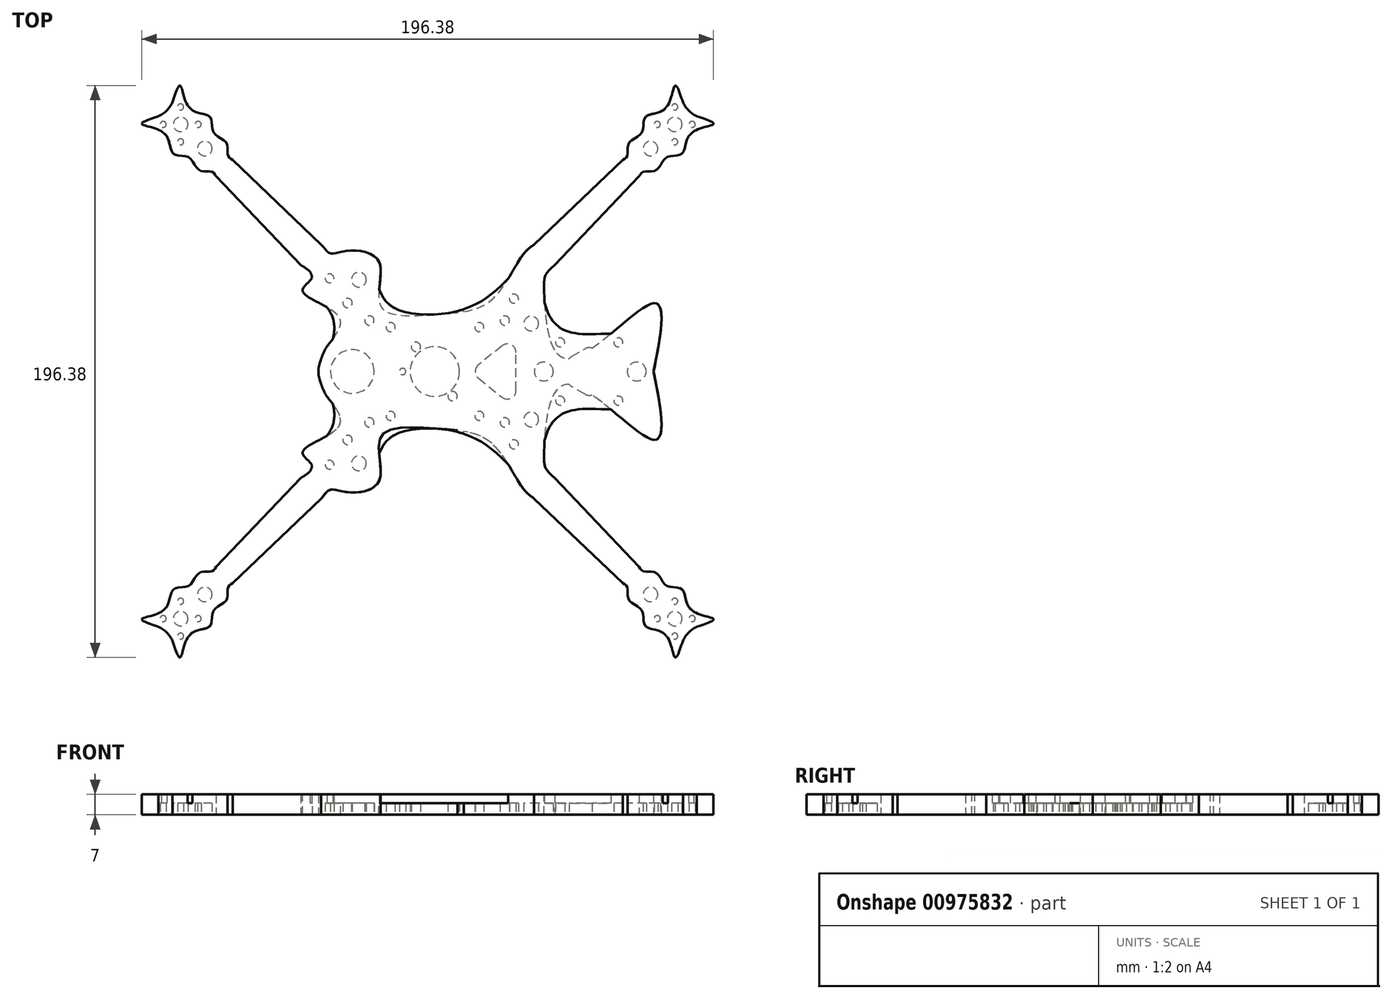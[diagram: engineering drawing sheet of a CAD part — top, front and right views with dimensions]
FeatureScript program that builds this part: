
annotation { "Feature Type Name" : "Feature", "Feature Type Description" : "" }
export const myFeature = defineFeature(function(context is Context, id is Id, definition is map)
    precondition{}
    {
        {
            var Q0;
            Q0=qCreatedBy(makeId("Top.planeOp"),FACE);
            var sketch = newSketch(context, id + "F0", { "sketchPlane" : qUnion([Q0])});
            skCircle(sketch, "E0", {"center": v(-32.76, 31.1) * mm, "radius": 1.46 * mm});
            skCircle(sketch, "E1", {"center": v(-32.76, -31.1) * mm, "radius": 1.46 * mm});
            skCircle(sketch, "E2", {"center": v(28.8, -24.3) * mm, "radius": 1.5 * mm});
            skCircle(sketch, "E3", {"center": v(28.8, 24.3) * mm, "radius": 1.5 * mm});
            skCircle(sketch, "E4", {"center": v(38.75, 0) * mm, "radius": 3.16 * mm});
            skCircle(sketch, "E5", {"center": v(69.82, 0) * mm, "radius": 3.16 * mm});
            skCircle(sketch, "E6", {"center": v(63.67, -9.72) * mm, "radius": 1.5 * mm});
            skCircle(sketch, "E7", {"center": v(63.67, 9.72) * mm, "radius": 1.5 * mm});
            skCircle(sketch, "E8", {"center": v(44.23, 9.72) * mm, "radius": 1.5 * mm});
            skCircle(sketch, "E9", {"center": v(44.23, -9.72) * mm, "radius": 1.5 * mm});
            skCircle(sketch, "E10", {"center": v(-76.65, 82.48) * mm, "radius": 1.02 * mm});
            skCircle(sketch, "E11", {"center": v(-82.48, 88.32) * mm, "radius": 1.02 * mm});
            skCircle(sketch, "E12", {"center": v(-88.32, 82.48) * mm, "radius": 1.02 * mm});
            skCircle(sketch, "E13", {"center": v(-82.48, 82.48) * mm, "radius": 2.43 * mm});
            skCircle(sketch, "E14", {"center": v(-82.48, 76.65) * mm, "radius": 1.02 * mm});
            skCircle(sketch, "E15", {"center": v(-74.4, 74.4) * mm, "radius": 2.43 * mm});
            skCircle(sketch, "E16", {"center": v(88.32, 82.48) * mm, "radius": 1.02 * mm});
            skCircle(sketch, "E17", {"center": v(82.48, 88.32) * mm, "radius": 1.02 * mm});
            skCircle(sketch, "E18", {"center": v(76.65, 82.48) * mm, "radius": 1.02 * mm});
            skCircle(sketch, "E19", {"center": v(82.48, 82.48) * mm, "radius": 2.43 * mm});
            skCircle(sketch, "E20", {"center": v(74.4, 74.4) * mm, "radius": 2.43 * mm});
            skCircle(sketch, "E21", {"center": v(82.48, 76.65) * mm, "radius": 1.02 * mm});
            skCircle(sketch, "E22", {"center": v(76.65, -82.48) * mm, "radius": 1.02 * mm});
            skCircle(sketch, "E23", {"center": v(74.4, -74.4) * mm, "radius": 2.43 * mm});
            skCircle(sketch, "E24", {"center": v(82.48, -76.65) * mm, "radius": 1.02 * mm});
            skCircle(sketch, "E25", {"center": v(82.48, -82.48) * mm, "radius": 2.43 * mm});
            skCircle(sketch, "E26", {"center": v(88.32, -82.48) * mm, "radius": 1.02 * mm});
            skCircle(sketch, "E27", {"center": v(82.48, -88.32) * mm, "radius": 1.02 * mm});
            skCircle(sketch, "E28", {"center": v(-25.16, 0) * mm, "radius": 7.3 * mm});
            skCircle(sketch, "E29", {"center": v(17.68, -15.25) * mm, "radius": 1.5 * mm});
            skCircle(sketch, "E30", {"center": v(17.68, 15.25) * mm, "radius": 1.5 * mm});
            skCircle(sketch, "E31", {"center": v(-12.82, 15.25) * mm, "radius": 1.5 * mm});
            skCircle(sketch, "E32", {"center": v(-12.82, -15.25) * mm, "radius": 1.5 * mm});
            skCircle(sketch, "E33", {"center": v(-26.73, 22.84) * mm, "radius": 1.6 * mm});
            skCircle(sketch, "E34", {"center": v(-26.73, -22.84) * mm, "radius": 1.6 * mm});
            skCircle(sketch, "E35", {"center": v(-22.98, -30.67) * mm, "radius": 2.47 * mm});
            skCircle(sketch, "E36", {"center": v(34.56, -16) * mm, "radius": 2.47 * mm});
            skCircle(sketch, "E37", {"center": v(34.56, 16) * mm, "radius": 2.47 * mm});
            skCircle(sketch, "E38", {"center": v(-22.98, 30.67) * mm, "radius": 2.47 * mm});
            skCircle(sketch, "E39", {"center": v(-19.44, 17.01) * mm, "radius": 1.6 * mm});
            skCircle(sketch, "E40", {"center": v(25.76, 17.01) * mm, "radius": 1.6 * mm});
            skCircle(sketch, "E41", {"center": v(25.76, -17.01) * mm, "radius": 1.6 * mm});
            skCircle(sketch, "E42", {"center": v(-19.44, -17.01) * mm, "radius": 1.6 * mm});
            skCircle(sketch, "E43", {"center": v(-74.4, -74.4) * mm, "radius": 2.43 * mm});
            skCircle(sketch, "E44", {"center": v(-82.48, -88.32) * mm, "radius": 1.02 * mm});
            skCircle(sketch, "E45", {"center": v(-88.32, -82.48) * mm, "radius": 1.02 * mm});
            skCircle(sketch, "E46", {"center": v(-82.48, -76.65) * mm, "radius": 1.02 * mm});
            skCircle(sketch, "E47", {"center": v(-82.48, -82.48) * mm, "radius": 2.43 * mm});
            skCircle(sketch, "E48", {"center": v(-76.65, -82.48) * mm, "radius": 1.02 * mm});
            skLineSegment(sketch, "E49", {"start": v(0.97, -7.58) * mm, "end": v(-3.4, -5.05) * mm, "construction": true});
            skLineSegment(sketch, "E50", {"start": v(8.26, -5.05) * mm, "end": v(3.89, -7.58) * mm, "construction": true});
            skLineSegment(sketch, "E51", {"start": v(9.72, 2.53) * mm, "end": v(9.72, -2.53) * mm, "construction": true});
            skLineSegment(sketch, "E52", {"start": v(3.89, 7.58) * mm, "end": v(8.26, 5.05) * mm, "construction": true});
            skLineSegment(sketch, "E53", {"start": v(-3.4, 5.05) * mm, "end": v(0.97, 7.58) * mm, "construction": true});
            skLineSegment(sketch, "E54", {"start": v(-4.86, -2.53) * mm, "end": v(-4.86, 2.53) * mm, "construction": true});
            skLineSegment(sketch, "E55", {"start": v(-42.4, 35.54) * mm, "end": v(-70.64, 65.14) * mm});
            skLineSegment(sketch, "E56", {"start": v(-65.14, 70.64) * mm, "end": v(-35.54, 42.4) * mm});
            skLineSegment(sketch, "E57", {"start": v(35.54, 42.4) * mm, "end": v(65.14, 70.64) * mm});
            skLineSegment(sketch, "E58", {"start": v(70.64, 65.14) * mm, "end": v(42.4, 35.54) * mm});
            skLineSegment(sketch, "E59", {"start": v(42.4, -35.54) * mm, "end": v(70.64, -65.14) * mm});
            skLineSegment(sketch, "E60", {"start": v(65.14, -70.64) * mm, "end": v(35.54, -42.4) * mm});
            skLineSegment(sketch, "E61", {"start": v(-35.54, -42.4) * mm, "end": v(-65.14, -70.64) * mm});
            skLineSegment(sketch, "E62", {"start": v(-70.64, -65.14) * mm, "end": v(-42.4, -35.54) * mm});
            skLineSegment(sketch, "E63", {"start": v(52.5, -7.58) * mm, "end": v(48.12, -5.05) * mm});
            skLineSegment(sketch, "E64", {"start": v(59.78, -5.05) * mm, "end": v(55.4, -7.58) * mm});
            skLineSegment(sketch, "E65", {"start": v(61.24, 2.53) * mm, "end": v(61.24, -2.53) * mm});
            skLineSegment(sketch, "E66", {"start": v(55.4, 7.58) * mm, "end": v(59.78, 5.05) * mm});
            skLineSegment(sketch, "E67", {"start": v(48.12, 5.05) * mm, "end": v(52.5, 7.58) * mm});
            skLineSegment(sketch, "E68", {"start": v(46.66, -2.53) * mm, "end": v(46.66, 2.53) * mm});
            skLineSegment(sketch, "E69", {"start": v(24.77, 8.56) * mm, "end": v(16.99, 2.27) * mm});
            skLineSegment(sketch, "E70", {"start": v(16.99, -2.27) * mm, "end": v(24.77, -8.56) * mm});
            skLineSegment(sketch, "E71", {"start": v(29.52, -6.29) * mm, "end": v(29.52, 6.29) * mm});
            skArc(sketch, "E72", {"start": v(-4.86, -2.53) * mm, "mid": v(-4.47, -3.98) * mm, "end": v(-3.4, -5.05) * mm, "construction": true});
            skArc(sketch, "E73", {"start": v(0.97, -7.58) * mm, "mid": v(2.43, -7.97) * mm, "end": v(3.89, -7.58) * mm, "construction": true});
            skArc(sketch, "E74", {"start": v(8.26, -5.05) * mm, "mid": v(9.33, -3.98) * mm, "end": v(9.72, -2.53) * mm, "construction": true});
            skArc(sketch, "E75", {"start": v(9.72, 2.53) * mm, "mid": v(9.33, 3.98) * mm, "end": v(8.26, 5.05) * mm, "construction": true});
            skArc(sketch, "E76", {"start": v(3.89, 7.58) * mm, "mid": v(2.43, 7.97) * mm, "end": v(0.97, 7.58) * mm, "construction": true});
            skArc(sketch, "E77", {"start": v(-3.4, 5.05) * mm, "mid": v(-4.47, 3.98) * mm, "end": v(-4.86, 2.53) * mm, "construction": true});
            skArc(sketch, "E78", {"start": v(-89.87, 85.21) * mm, "mid": v(-87.13, 87.13) * mm, "end": v(-85.21, 89.87) * mm});
            skArc(sketch, "E79", {"start": v(85.21, 89.87) * mm, "mid": v(87.13, 87.13) * mm, "end": v(89.87, 85.21) * mm});
            skArc(sketch, "E80", {"start": v(89.87, -85.21) * mm, "mid": v(87.13, -87.13) * mm, "end": v(85.21, -89.87) * mm});
            skArc(sketch, "E81", {"start": v(-85.21, -89.87) * mm, "mid": v(-87.13, -87.13) * mm, "end": v(-89.87, -85.21) * mm});
            skArc(sketch, "E82", {"start": v(-35.56, 4.15) * mm, "mid": v(-36.49, 0) * mm, "end": v(-35.56, -4.15) * mm});
            skArc(sketch, "E83", {"start": v(46.66, -2.53) * mm, "mid": v(47.05, -3.98) * mm, "end": v(48.12, -5.05) * mm});
            skArc(sketch, "E84", {"start": v(52.5, -7.58) * mm, "mid": v(53.95, -7.97) * mm, "end": v(55.4, -7.58) * mm});
            skArc(sketch, "E85", {"start": v(59.78, -5.05) * mm, "mid": v(60.85, -3.98) * mm, "end": v(61.24, -2.53) * mm});
            skArc(sketch, "E86", {"start": v(61.24, 2.53) * mm, "mid": v(60.85, 3.98) * mm, "end": v(59.78, 5.05) * mm});
            skArc(sketch, "E87", {"start": v(55.4, 7.58) * mm, "mid": v(53.95, 7.97) * mm, "end": v(52.5, 7.58) * mm});
            skArc(sketch, "E88", {"start": v(48.12, 5.05) * mm, "mid": v(47.05, 3.98) * mm, "end": v(46.66, 2.53) * mm});
            skArc(sketch, "E89", {"start": v(29.52, 6.29) * mm, "mid": v(27.86, 8.92) * mm, "end": v(24.77, 8.56) * mm});
            skArc(sketch, "E90", {"start": v(16.99, 2.27) * mm, "mid": v(15.9, 0) * mm, "end": v(16.99, -2.27) * mm});
            skArc(sketch, "E91", {"start": v(24.77, -8.56) * mm, "mid": v(27.86, -8.92) * mm, "end": v(29.52, -6.29) * mm});
            skFitSpline(sketch, "E92", {"points": [v(-70.64, 65.14) * mm, v(-72.1, 66.67) * mm, v(-76.27, 67.2) * mm, v(-79.78, 71.48) * mm, v(-84.93, 72.72) * mm, v(-87.81, 79.4) * mm, v(-95.41, 82.6) * mm, v(-89.87, 85.21) * mm]});
            skFitSpline(sketch, "E93", {"points": [v(-85.21, 89.87) * mm, v(-82.6, 95.41) * mm, v(-79.4, 87.81) * mm, v(-72.72, 84.93) * mm, v(-71.48, 79.78) * mm, v(-67.2, 76.27) * mm, v(-66.67, 72.1) * mm, v(-65.14, 70.64) * mm]});
            skFitSpline(sketch, "E94", {"points": [v(-35.53, 42.41) * mm, v(-32.44, 39.47) * mm, v(-27.5, 40.23) * mm, v(-16.3, 36.82) * mm, v(-15.63, 21.83) * mm, v(3.2, 19.1) * mm, v(21.3, 23.94) * mm, v(31.5, 38.64) * mm, v(35.55, 42.52) * mm]});
            skFitSpline(sketch, "E95", {"points": [v(65.14, 70.64) * mm, v(66.67, 72.1) * mm, v(67.2, 76.27) * mm, v(71.48, 79.78) * mm, v(72.72, 84.93) * mm, v(79.4, 87.81) * mm, v(82.6, 95.41) * mm, v(85.21, 89.87) * mm]});
            skFitSpline(sketch, "E96", {"points": [v(89.87, 85.21) * mm, v(95.41, 82.6) * mm, v(87.81, 79.4) * mm, v(84.93, 72.72) * mm, v(79.78, 71.48) * mm, v(76.27, 67.2) * mm, v(72.1, 66.67) * mm, v(70.64, 65.14) * mm]});
            skFitSpline(sketch, "E97", {"points": [v(42.4, 35.54) * mm, v(39.6, 32.6) * mm, v(38.88, 26.27) * mm, v(46.07, 4.37) * mm, v(75.44, 22.8) * mm, v(75.44, 0) * mm]});
            skFitSpline(sketch, "E98", {"points": [v(75.44, 0) * mm, v(75.44, -22.8) * mm, v(46.07, -4.37) * mm, v(38.88, -26.27) * mm, v(39.6, -32.6) * mm, v(42.4, -35.54) * mm]});
            skFitSpline(sketch, "E99", {"points": [v(70.64, -65.14) * mm, v(72.1, -66.67) * mm, v(76.27, -67.2) * mm, v(79.78, -71.48) * mm, v(84.93, -72.72) * mm, v(87.81, -79.4) * mm, v(95.41, -82.6) * mm, v(89.87, -85.21) * mm]});
            skFitSpline(sketch, "E100", {"points": [v(85.21, -89.87) * mm, v(82.6, -95.41) * mm, v(79.4, -87.81) * mm, v(72.72, -84.93) * mm, v(71.48, -79.78) * mm, v(67.2, -76.27) * mm, v(66.67, -72.1) * mm, v(65.14, -70.64) * mm]});
            skFitSpline(sketch, "E101", {"points": [v(35.54, -42.4) * mm, v(31.48, -38.53) * mm, v(21.27, -23.86) * mm, v(3.16, -19.04) * mm, v(-15.67, -21.8) * mm, v(-16.31, -36.79) * mm, v(-27.5, -40.21) * mm, v(-32.45, -39.46) * mm, v(-35.54, -42.4) * mm]});
            skFitSpline(sketch, "E102", {"points": [v(-65.14, -70.64) * mm, v(-66.67, -72.1) * mm, v(-67.2, -76.27) * mm, v(-71.48, -79.78) * mm, v(-72.72, -84.93) * mm, v(-79.4, -87.81) * mm, v(-82.6, -95.41) * mm, v(-85.21, -89.87) * mm]});
            skFitSpline(sketch, "E103", {"points": [v(-89.87, -85.21) * mm, v(-95.41, -82.6) * mm, v(-87.81, -79.4) * mm, v(-84.93, -72.72) * mm, v(-79.78, -71.48) * mm, v(-76.27, -67.2) * mm, v(-72.1, -66.67) * mm, v(-70.64, -65.14) * mm]});
            skFitSpline(sketch, "E104", {"points": [v(-42.4, -35.54) * mm, v(-38.56, -31.5) * mm, v(-41.74, -26.82) * mm, v(-29.39, -17.9) * mm, v(-33.52, -8.47) * mm, v(-35.56, -4.15) * mm]});
            skFitSpline(sketch, "E105", {"points": [v(-35.56, 4.15) * mm, v(-33.52, 8.47) * mm, v(-29.39, 17.9) * mm, v(-41.74, 26.82) * mm, v(-38.56, 31.5) * mm, v(-42.4, 35.54) * mm]});
            skLineSegment(sketch, "E106", {"start": v(-1.94, 2.53) * mm, "end": v(6.8, -2.53) * mm, "construction": true});
            skLineSegment(sketch, "E107", {"start": v(-1.94, -2.53) * mm, "end": v(6.8, 2.53) * mm, "construction": true});
            skLineSegment(sketch, "E108", {"start": v(2.43, 5.05) * mm, "end": v(2.43, -5.05) * mm, "construction": true});
            skPoint(sketch, "E109", {"position": v(2.43, 0) * mm});
            skCircle(sketch, "E110", {"center": v(2.43, 0) * mm, "radius": 8.5 * mm});
            skLineSegment(sketch, "E111", {"start": v(-12.82, 15.25) * mm, "end": v(17.68, -15.25) * mm, "construction": true});
            skLineSegment(sketch, "E112", {"start": v(-12.82, -15.25) * mm, "end": v(17.68, 15.25) * mm, "construction": true});
            skLineSegment(sketch, "E113", {"start": v(-12.82, 15.25) * mm, "end": v(17.68, 15.25) * mm, "construction": true});
            skLineSegment(sketch, "E114", {"start": v(17.68, 15.25) * mm, "end": v(17.68, -15.25) * mm, "construction": true});
            skLineSegment(sketch, "E115.bottom", {"start": v(-6.59, 11.05) * mm, "end": v(13.31, 11.05) * mm, "construction": true});
            skLineSegment(sketch, "E115.top", {"start": v(-6.59, -11.05) * mm, "end": v(13.31, -11.05) * mm, "construction": true});
            skLineSegment(sketch, "E115.left", {"start": v(-6.59, 11.05) * mm, "end": v(-6.59, -11.05) * mm, "construction": true});
            skLineSegment(sketch, "E115.right", {"start": v(13.31, 11.05) * mm, "end": v(13.31, -11.05) * mm, "construction": true});
            skPoint(sketch, "E116", {"position": v(-6.59, 0) * mm});
            skCircle(sketch, "E117", {"center": v(-4.05, 8.5) * mm, "radius": 1.6 * mm});
            skCircle(sketch, "E118", {"center": v(8.55, -8.5) * mm, "radius": 1.6 * mm});
            skPoint(sketch, "E119", {"position": v(-14.67, 26.96) * mm});
            skPoint(sketch, "E120", {"position": v(-14.67, -26.85) * mm});
            skLineSegment(sketch, "E121", {"start": v(-14.67, 26.96) * mm, "end": v(-14.67, -26.85) * mm, "construction": true});
            skFitSpline(sketch, "E122", {"points": [v(-14.67, 26.96) * mm, v(12.39, 26.96) * mm, v(35.54, 42.4) * mm], "startDerivative": vector(9.65, -21.34) * mm, "endDerivative": vector(35.23, 30.54) * mm});
            skFitSpline(sketch, "E123.MirrorCS", {"points": [v(-14.67, -26.96) * mm, v(12.39, -26.96) * mm, v(35.54, -42.4) * mm], "startDerivative": vector(9.65, 21.34) * mm, "endDerivative": vector(35.23, -30.54) * mm});
            skCircle(sketch, "E124", {"center": v(7.43, 20) * mm, "radius": 1.1 * mm});
            skCircle(sketch, "E125", {"center": v(-12.57, 0) * mm, "radius": 1.1 * mm});
            skCircle(sketch, "E126", {"center": v(7.43, -20) * mm, "radius": 1.1 * mm});
            skSolve(sketch);
        }
        {
            var Q0;
            Q0=qCreatedBy(makeId("Top.planeOp"),FACE);
            var sketch = newSketch(context, id + "F1", { "sketchPlane" : qUnion([Q0])});
            skCircle(sketch, "E127", {"center": v(-33.7, 32) * mm, "radius": 1.5 * mm});
            skCircle(sketch, "E128", {"center": v(-33.7, -32) * mm, "radius": 1.5 * mm});
            skCircle(sketch, "E129", {"center": v(29.62, -25) * mm, "radius": 1.55 * mm});
            skCircle(sketch, "E130", {"center": v(29.62, 25) * mm, "radius": 1.55 * mm});
            skCircle(sketch, "E131", {"center": v(39.86, 0) * mm, "radius": 3.25 * mm});
            skCircle(sketch, "E132", {"center": v(71.83, 0) * mm, "radius": 3.25 * mm});
            skCircle(sketch, "E133", {"center": v(65.5, -10) * mm, "radius": 1.55 * mm});
            skCircle(sketch, "E134", {"center": v(65.5, 10) * mm, "radius": 1.55 * mm});
            skCircle(sketch, "E135", {"center": v(45.5, 10) * mm, "radius": 1.55 * mm});
            skCircle(sketch, "E136", {"center": v(45.5, -10) * mm, "radius": 1.55 * mm});
            skCircle(sketch, "E137", {"center": v(-78.85, 84.85) * mm, "radius": 1.05 * mm});
            skCircle(sketch, "E138", {"center": v(-84.85, 90.85) * mm, "radius": 1.05 * mm});
            skCircle(sketch, "E139", {"center": v(-90.85, 84.85) * mm, "radius": 1.05 * mm});
            skCircle(sketch, "E140", {"center": v(-84.85, 84.85) * mm, "radius": 2.5 * mm});
            skCircle(sketch, "E141", {"center": v(-84.85, 78.85) * mm, "radius": 1.05 * mm});
            skCircle(sketch, "E142", {"center": v(-76.54, 76.54) * mm, "radius": 2.5 * mm});
            skCircle(sketch, "E143", {"center": v(90.85, 84.85) * mm, "radius": 1.05 * mm});
            skCircle(sketch, "E144", {"center": v(84.85, 90.85) * mm, "radius": 1.05 * mm});
            skCircle(sketch, "E145", {"center": v(78.85, 84.85) * mm, "radius": 1.05 * mm});
            skCircle(sketch, "E146", {"center": v(84.85, 84.85) * mm, "radius": 2.5 * mm});
            skCircle(sketch, "E147", {"center": v(76.54, 76.54) * mm, "radius": 2.5 * mm});
            skCircle(sketch, "E148", {"center": v(84.85, 78.85) * mm, "radius": 1.05 * mm});
            skCircle(sketch, "E149", {"center": v(78.85, -84.85) * mm, "radius": 1.05 * mm});
            skCircle(sketch, "E150", {"center": v(76.54, -76.54) * mm, "radius": 2.5 * mm});
            skCircle(sketch, "E151", {"center": v(84.85, -78.85) * mm, "radius": 1.05 * mm});
            skCircle(sketch, "E152", {"center": v(84.85, -84.85) * mm, "radius": 2.5 * mm});
            skCircle(sketch, "E153", {"center": v(90.85, -84.85) * mm, "radius": 1.05 * mm});
            skCircle(sketch, "E154", {"center": v(84.85, -90.85) * mm, "radius": 1.05 * mm});
            skCircle(sketch, "E155", {"center": v(-25.89, 0) * mm, "radius": 7.5 * mm});
            skCircle(sketch, "E156", {"center": v(17.75, -15.25) * mm, "radius": 1.55 * mm});
            skCircle(sketch, "E157", {"center": v(17.75, 15.25) * mm, "radius": 1.55 * mm});
            skCircle(sketch, "E158", {"center": v(-12.75, 15.25) * mm, "radius": 1.55 * mm});
            skCircle(sketch, "E159", {"center": v(-12.75, -15.25) * mm, "radius": 1.55 * mm});
            skCircle(sketch, "E160", {"center": v(-27.5, 23.5) * mm, "radius": 1.6 * mm});
            skCircle(sketch, "E161", {"center": v(-27.5, -23.5) * mm, "radius": 1.6 * mm});
            skCircle(sketch, "E162", {"center": v(-23.64, -31.55) * mm, "radius": 2.54 * mm});
            skCircle(sketch, "E163", {"center": v(35.56, -16.47) * mm, "radius": 2.54 * mm});
            skCircle(sketch, "E164", {"center": v(35.56, 16.47) * mm, "radius": 2.54 * mm});
            skCircle(sketch, "E165", {"center": v(-23.64, 31.55) * mm, "radius": 2.54 * mm});
            skCircle(sketch, "E166", {"center": v(-20, 17.5) * mm, "radius": 1.6 * mm});
            skCircle(sketch, "E167", {"center": v(26.5, 17.5) * mm, "radius": 1.6 * mm});
            skCircle(sketch, "E168", {"center": v(26.5, -17.5) * mm, "radius": 1.6 * mm});
            skCircle(sketch, "E169", {"center": v(-20, -17.5) * mm, "radius": 1.6 * mm});
            skCircle(sketch, "E170", {"center": v(-76.54, -76.54) * mm, "radius": 2.5 * mm});
            skCircle(sketch, "E171", {"center": v(-84.85, -90.85) * mm, "radius": 1.05 * mm});
            skCircle(sketch, "E172", {"center": v(-90.85, -84.85) * mm, "radius": 1.05 * mm});
            skCircle(sketch, "E173", {"center": v(-84.85, -78.85) * mm, "radius": 1.05 * mm});
            skCircle(sketch, "E174", {"center": v(-84.85, -84.85) * mm, "radius": 2.5 * mm});
            skCircle(sketch, "E175", {"center": v(-78.85, -84.85) * mm, "radius": 1.05 * mm});
            skLineSegment(sketch, "E176", {"start": v(1, -7.8) * mm, "end": v(-3.5, -5.2) * mm, "construction": true});
            skLineSegment(sketch, "E177", {"start": v(8.5, -5.2) * mm, "end": v(4, -7.8) * mm, "construction": true});
            skLineSegment(sketch, "E178", {"start": v(10, 2.6) * mm, "end": v(10, -2.6) * mm, "construction": true});
            skLineSegment(sketch, "E179", {"start": v(4, 7.8) * mm, "end": v(8.5, 5.2) * mm, "construction": true});
            skLineSegment(sketch, "E180", {"start": v(-3.5, 5.2) * mm, "end": v(1, 7.8) * mm, "construction": true});
            skLineSegment(sketch, "E181", {"start": v(-5, -2.6) * mm, "end": v(-5, 2.6) * mm, "construction": true});
            skLineSegment(sketch, "E182", {"start": v(-43.63, 36.56) * mm, "end": v(-72.67, 67) * mm});
            skLineSegment(sketch, "E183", {"start": v(-67, 72.67) * mm, "end": v(-36.56, 43.63) * mm});
            skLineSegment(sketch, "E184", {"start": v(36.56, 43.63) * mm, "end": v(67, 72.67) * mm});
            skLineSegment(sketch, "E185", {"start": v(72.67, 67) * mm, "end": v(43.63, 36.56) * mm});
            skLineSegment(sketch, "E186", {"start": v(43.63, -36.56) * mm, "end": v(72.67, -67) * mm});
            skLineSegment(sketch, "E187", {"start": v(67, -72.67) * mm, "end": v(36.56, -43.63) * mm});
            skLineSegment(sketch, "E188", {"start": v(-36.56, -43.63) * mm, "end": v(-67, -72.67) * mm});
            skLineSegment(sketch, "E189", {"start": v(-72.67, -67) * mm, "end": v(-43.63, -36.56) * mm});
            skLineSegment(sketch, "E190", {"start": v(54, -7.8) * mm, "end": v(49.5, -5.2) * mm});
            skLineSegment(sketch, "E191", {"start": v(61.5, -5.2) * mm, "end": v(57, -7.8) * mm});
            skLineSegment(sketch, "E192", {"start": v(63, 2.6) * mm, "end": v(63, -2.6) * mm});
            skLineSegment(sketch, "E193", {"start": v(57, 7.8) * mm, "end": v(61.5, 5.2) * mm});
            skLineSegment(sketch, "E194", {"start": v(49.5, 5.2) * mm, "end": v(54, 7.8) * mm});
            skLineSegment(sketch, "E195", {"start": v(48, -2.6) * mm, "end": v(48, 2.6) * mm});
            skLineSegment(sketch, "E196", {"start": v(25.48, 8.8) * mm, "end": v(17.47, 2.33) * mm});
            skLineSegment(sketch, "E197", {"start": v(17.47, -2.33) * mm, "end": v(25.48, -8.8) * mm});
            skLineSegment(sketch, "E198", {"start": v(30.37, -6.47) * mm, "end": v(30.37, 6.47) * mm});
            skArc(sketch, "E199", {"start": v(-5, -2.6) * mm, "mid": v(-4.6, -4.1) * mm, "end": v(-3.5, -5.2) * mm, "construction": true});
            skArc(sketch, "E200", {"start": v(1, -7.8) * mm, "mid": v(2.5, -8.2) * mm, "end": v(4, -7.8) * mm, "construction": true});
            skArc(sketch, "E201", {"start": v(8.5, -5.2) * mm, "mid": v(9.6, -4.1) * mm, "end": v(10, -2.6) * mm, "construction": true});
            skArc(sketch, "E202", {"start": v(10, 2.6) * mm, "mid": v(9.6, 4.1) * mm, "end": v(8.5, 5.2) * mm, "construction": true});
            skArc(sketch, "E203", {"start": v(4, 7.8) * mm, "mid": v(2.5, 8.2) * mm, "end": v(1, 7.8) * mm, "construction": true});
            skArc(sketch, "E204", {"start": v(-3.5, 5.2) * mm, "mid": v(-4.6, 4.1) * mm, "end": v(-5, 2.6) * mm, "construction": true});
            skArc(sketch, "E205", {"start": v(-92.45, 87.66) * mm, "mid": v(-89.64, 89.64) * mm, "end": v(-87.66, 92.45) * mm});
            skArc(sketch, "E206", {"start": v(87.66, 92.45) * mm, "mid": v(89.64, 89.64) * mm, "end": v(92.45, 87.66) * mm});
            skArc(sketch, "E207", {"start": v(92.45, -87.66) * mm, "mid": v(89.64, -89.64) * mm, "end": v(87.66, -92.45) * mm});
            skArc(sketch, "E208", {"start": v(-87.66, -92.45) * mm, "mid": v(-89.64, -89.64) * mm, "end": v(-92.45, -87.66) * mm});
            skArc(sketch, "E209", {"start": v(-36.58, 4.27) * mm, "mid": v(-37.53, 0) * mm, "end": v(-36.58, -4.27) * mm});
            skArc(sketch, "E210", {"start": v(48, -2.6) * mm, "mid": v(48.4, -4.1) * mm, "end": v(49.5, -5.2) * mm});
            skArc(sketch, "E211", {"start": v(54, -7.8) * mm, "mid": v(55.5, -8.2) * mm, "end": v(57, -7.8) * mm});
            skArc(sketch, "E212", {"start": v(61.5, -5.2) * mm, "mid": v(62.6, -4.1) * mm, "end": v(63, -2.6) * mm});
            skArc(sketch, "E213", {"start": v(63, 2.6) * mm, "mid": v(62.6, 4.1) * mm, "end": v(61.5, 5.2) * mm});
            skArc(sketch, "E214", {"start": v(57, 7.8) * mm, "mid": v(55.5, 8.2) * mm, "end": v(54, 7.8) * mm});
            skArc(sketch, "E215", {"start": v(49.5, 5.2) * mm, "mid": v(48.4, 4.1) * mm, "end": v(48, 2.6) * mm});
            skArc(sketch, "E216", {"start": v(30.37, 6.47) * mm, "mid": v(28.66, 9.18) * mm, "end": v(25.48, 8.8) * mm});
            skArc(sketch, "E217", {"start": v(17.47, 2.33) * mm, "mid": v(16.36, 0) * mm, "end": v(17.47, -2.33) * mm});
            skArc(sketch, "E218", {"start": v(25.48, -8.8) * mm, "mid": v(28.66, -9.18) * mm, "end": v(30.37, -6.47) * mm});
            skFitSpline(sketch, "E219", {"points": [v(-72.67, 67) * mm, v(-74.17, 68.59) * mm, v(-78.46, 69.14) * mm, v(-82.07, 73.54) * mm, v(-87.37, 74.8) * mm, v(-90.34, 81.69) * mm, v(-98.15, 84.97) * mm, v(-92.45, 87.66) * mm]});
            skFitSpline(sketch, "E220", {"points": [v(-87.66, 92.45) * mm, v(-84.97, 98.15) * mm, v(-81.69, 90.34) * mm, v(-74.8, 87.37) * mm, v(-73.54, 82.07) * mm, v(-69.14, 78.46) * mm, v(-68.59, 74.17) * mm, v(-67, 72.67) * mm]});
            skFitSpline(sketch, "E221", {"points": [v(-36.56, 43.63) * mm, v(-33.38, 40.6) * mm, v(-28.3, 41.37) * mm, v(-16.78, 37.85) * mm, v(-16.12, 22.42) * mm, v(3.25, 19.6) * mm, v(21.88, 24.54) * mm, v(32.38, 39.64) * mm, v(36.56, 43.63) * mm]});
            skFitSpline(sketch, "E222", {"points": [v(67, 72.67) * mm, v(68.59, 74.17) * mm, v(69.14, 78.46) * mm, v(73.54, 82.07) * mm, v(74.8, 87.37) * mm, v(81.69, 90.34) * mm, v(84.97, 98.15) * mm, v(87.66, 92.45) * mm]});
            skFitSpline(sketch, "E223", {"points": [v(92.45, 87.66) * mm, v(98.15, 84.97) * mm, v(90.34, 81.69) * mm, v(87.37, 74.8) * mm, v(82.07, 73.54) * mm, v(78.46, 69.14) * mm, v(74.17, 68.59) * mm, v(72.67, 67) * mm]});
            skFitSpline(sketch, "E224", {"points": [v(43.63, 36.56) * mm, v(40.74, 33.53) * mm, v(40, 27.02) * mm, v(47.4, 4.5) * mm, v(77.6, 23.46) * mm, v(77.6, 0) * mm]});
            skFitSpline(sketch, "E225", {"points": [v(77.6, 0) * mm, v(77.6, -23.46) * mm, v(47.4, -4.5) * mm, v(40, -27.02) * mm, v(40.74, -33.53) * mm, v(43.63, -36.56) * mm]});
            skFitSpline(sketch, "E226", {"points": [v(72.67, -67) * mm, v(74.17, -68.59) * mm, v(78.46, -69.14) * mm, v(82.07, -73.54) * mm, v(87.37, -74.8) * mm, v(90.34, -81.69) * mm, v(98.15, -84.97) * mm, v(92.45, -87.66) * mm]});
            skFitSpline(sketch, "E227", {"points": [v(87.66, -92.45) * mm, v(84.97, -98.15) * mm, v(81.69, -90.34) * mm, v(74.8, -87.37) * mm, v(73.54, -82.07) * mm, v(69.14, -78.46) * mm, v(68.59, -74.17) * mm, v(67, -72.67) * mm]});
            skFitSpline(sketch, "E228", {"points": [v(36.56, -43.63) * mm, v(32.38, -39.64) * mm, v(21.88, -24.54) * mm, v(3.25, -19.6) * mm, v(-16.12, -22.42) * mm, v(-16.78, -37.85) * mm, v(-28.3, -41.37) * mm, v(-33.38, -40.6) * mm, v(-36.56, -43.63) * mm]});
            skFitSpline(sketch, "E229", {"points": [v(-67, -72.67) * mm, v(-68.59, -74.17) * mm, v(-69.14, -78.46) * mm, v(-73.54, -82.07) * mm, v(-74.8, -87.37) * mm, v(-81.69, -90.34) * mm, v(-84.97, -98.15) * mm, v(-87.66, -92.45) * mm]});
            skFitSpline(sketch, "E230", {"points": [v(-92.45, -87.66) * mm, v(-98.15, -84.97) * mm, v(-90.34, -81.69) * mm, v(-87.37, -74.8) * mm, v(-82.07, -73.54) * mm, v(-78.46, -69.14) * mm, v(-74.17, -68.59) * mm, v(-72.67, -67) * mm]});
            skFitSpline(sketch, "E231", {"points": [v(-43.63, -36.56) * mm, v(-39.67, -32.4) * mm, v(-42.94, -27.6) * mm, v(-30.23, -18.41) * mm, v(-34.48, -8.7) * mm, v(-36.58, -4.27) * mm]});
            skFitSpline(sketch, "E232", {"points": [v(-36.58, 4.27) * mm, v(-34.48, 8.7) * mm, v(-30.23, 18.41) * mm, v(-42.94, 27.6) * mm, v(-39.67, 32.4) * mm, v(-43.63, 36.56) * mm]});
            skCircle(sketch, "E233.0", {"center": v(-4.05, 8.5) * mm, "radius": 1.6 * mm});
            skCircle(sketch, "E233.1", {"center": v(8.55, -8.5) * mm, "radius": 1.6 * mm});
            skCircle(sketch, "E233.2", {"center": v(2.43, 0) * mm, "radius": 8.5 * mm});
            skCircle(sketch, "E234", {"center": v(11.38, 20) * mm, "radius": 1.1 * mm});
            skCircle(sketch, "E235", {"center": v(11.38, -20) * mm, "radius": 1.1 * mm});
            skLineSegment(sketch, "E236", {"start": v(11.38, 20) * mm, "end": v(11.38, -20) * mm, "construction": true});
            skPoint(sketch, "E237", {"position": v(11.38, 0) * mm});
            skCircle(sketch, "E238", {"center": v(-8.62, 0) * mm, "radius": 1.1 * mm});
            skSolve(sketch);
        }
        {
            var Q0;
            Q0 = qSketchRegion(id + "F1", true);
            extrude(context, id + "F2", {"entities" : qUnion([Q0]), "depth" : 4 * mm, "offsetDistance" : 25 * mm});
        }
        {
            var Q0;
            Q0=makeQuery(id+"F2.opExtrude","CAP_FACE",FACE,{"disambiguationData":[OSD([sQuery(id+"F1.wireOp",EDGE,"E127"),sQuery(id+"F1.wireOp",EDGE,"E128"),sQuery(id+"F1.wireOp",EDGE,"E129"),sQuery(id+"F1.wireOp",EDGE,"E130"),sQuery(id+"F1.wireOp",EDGE,"E131"),sQuery(id+"F1.wireOp",EDGE,"E132"),sQuery(id+"F1.wireOp",EDGE,"E133"),sQuery(id+"F1.wireOp",EDGE,"E134"),sQuery(id+"F1.wireOp",EDGE,"E135"),sQuery(id+"F1.wireOp",EDGE,"E136"),sQuery(id+"F1.wireOp",EDGE,"E137"),sQuery(id+"F1.wireOp",EDGE,"E138"),sQuery(id+"F1.wireOp",EDGE,"E139"),sQuery(id+"F1.wireOp",EDGE,"E140"),sQuery(id+"F1.wireOp",EDGE,"E141"),sQuery(id+"F1.wireOp",EDGE,"E142"),sQuery(id+"F1.wireOp",EDGE,"E143"),sQuery(id+"F1.wireOp",EDGE,"E144"),sQuery(id+"F1.wireOp",EDGE,"E145"),sQuery(id+"F1.wireOp",EDGE,"E146"),sQuery(id+"F1.wireOp",EDGE,"E147"),sQuery(id+"F1.wireOp",EDGE,"E148"),sQuery(id+"F1.wireOp",EDGE,"E149"),sQuery(id+"F1.wireOp",EDGE,"E150"),sQuery(id+"F1.wireOp",EDGE,"E151"),sQuery(id+"F1.wireOp",EDGE,"E152"),sQuery(id+"F1.wireOp",EDGE,"E153"),sQuery(id+"F1.wireOp",EDGE,"E154"),sQuery(id+"F1.wireOp",EDGE,"E155"),sQuery(id+"F1.wireOp",EDGE,"E156"),sQuery(id+"F1.wireOp",EDGE,"E157"),sQuery(id+"F1.wireOp",EDGE,"E158"),sQuery(id+"F1.wireOp",EDGE,"E159"),sQuery(id+"F1.wireOp",EDGE,"E160"),sQuery(id+"F1.wireOp",EDGE,"E161"),sQuery(id+"F1.wireOp",EDGE,"E162"),sQuery(id+"F1.wireOp",EDGE,"E163"),sQuery(id+"F1.wireOp",EDGE,"E164"),sQuery(id+"F1.wireOp",EDGE,"E165"),sQuery(id+"F1.wireOp",EDGE,"E166"),sQuery(id+"F1.wireOp",EDGE,"E167"),sQuery(id+"F1.wireOp",EDGE,"E168"),sQuery(id+"F1.wireOp",EDGE,"E169"),sQuery(id+"F1.wireOp",EDGE,"E170"),sQuery(id+"F1.wireOp",EDGE,"E171"),sQuery(id+"F1.wireOp",EDGE,"E172"),sQuery(id+"F1.wireOp",EDGE,"E173"),sQuery(id+"F1.wireOp",EDGE,"E174"),sQuery(id+"F1.wireOp",EDGE,"E175"),sQuery(id+"F1.wireOp",EDGE,"E182"),sQuery(id+"F1.wireOp",EDGE,"E183"),sQuery(id+"F1.wireOp",EDGE,"E184"),sQuery(id+"F1.wireOp",EDGE,"E185"),sQuery(id+"F1.wireOp",EDGE,"E186"),sQuery(id+"F1.wireOp",EDGE,"E187"),sQuery(id+"F1.wireOp",EDGE,"E188"),sQuery(id+"F1.wireOp",EDGE,"E189"),sQuery(id+"F1.wireOp",EDGE,"E190"),sQuery(id+"F1.wireOp",EDGE,"E191"),sQuery(id+"F1.wireOp",EDGE,"E192"),sQuery(id+"F1.wireOp",EDGE,"E193"),sQuery(id+"F1.wireOp",EDGE,"E194"),sQuery(id+"F1.wireOp",EDGE,"E195"),sQuery(id+"F1.wireOp",EDGE,"E196"),sQuery(id+"F1.wireOp",EDGE,"E197"),sQuery(id+"F1.wireOp",EDGE,"E198"),sQuery(id+"F1.wireOp",EDGE,"E205"),sQuery(id+"F1.wireOp",EDGE,"E206"),sQuery(id+"F1.wireOp",EDGE,"E207"),sQuery(id+"F1.wireOp",EDGE,"E208"),sQuery(id+"F1.wireOp",EDGE,"E209"),sQuery(id+"F1.wireOp",EDGE,"E210"),sQuery(id+"F1.wireOp",EDGE,"E211"),sQuery(id+"F1.wireOp",EDGE,"E212"),sQuery(id+"F1.wireOp",EDGE,"E213"),sQuery(id+"F1.wireOp",EDGE,"E214"),sQuery(id+"F1.wireOp",EDGE,"E215"),sQuery(id+"F1.wireOp",EDGE,"E216"),sQuery(id+"F1.wireOp",EDGE,"E217"),sQuery(id+"F1.wireOp",EDGE,"E218"),sQuery(id+"F1.wireOp",EDGE,"E219"),sQuery(id+"F1.wireOp",EDGE,"E220"),sQuery(id+"F1.wireOp",EDGE,"E221"),sQuery(id+"F1.wireOp",EDGE,"E222"),sQuery(id+"F1.wireOp",EDGE,"E223"),sQuery(id+"F1.wireOp",EDGE,"E224"),sQuery(id+"F1.wireOp",EDGE,"E225"),sQuery(id+"F1.wireOp",EDGE,"E226"),sQuery(id+"F1.wireOp",EDGE,"E227"),sQuery(id+"F1.wireOp",EDGE,"E228"),sQuery(id+"F1.wireOp",EDGE,"E229"),sQuery(id+"F1.wireOp",EDGE,"E230"),sQuery(id+"F1.wireOp",EDGE,"E231"),sQuery(id+"F1.wireOp",EDGE,"E232"),sQuery(id+"F1.wireOp",EDGE,"E233.0"),sQuery(id+"F1.wireOp",EDGE,"E233.1"),sQuery(id+"F1.wireOp",EDGE,"E233.2"),sQuery(id+"F1.wireOp",EDGE,"E234"),sQuery(id+"F1.wireOp",EDGE,"E235"),sQuery(id+"F1.wireOp",EDGE,"E238")])],"isStart":false});
            var sketch = newSketch(context, id + "F3", { "sketchPlane" : qUnion([Q0])});
            skLineSegment(sketch, "E239", {"start": v(-68.08, 66.16) * mm, "end": v(-37.84, 35.91) * mm});
            skLineSegment(sketch, "E240", {"start": v(-37.84, 35.91) * mm, "end": v(-35.71, 38.03) * mm});
            skLineSegment(sketch, "E241", {"start": v(-35.71, 38.03) * mm, "end": v(-65.96, 68.28) * mm});
            skLineSegment(sketch, "E242", {"start": v(-65.96, 68.28) * mm, "end": v(-68.08, 66.16) * mm});
            skLineSegment(sketch, "E243.MirrorCS", {"start": v(-65.96, -68.28) * mm, "end": v(-68.08, -66.16) * mm});
            skLineSegment(sketch, "E244.MirrorCS", {"start": v(-35.71, -38.03) * mm, "end": v(-65.96, -68.28) * mm});
            skLineSegment(sketch, "E245.MirrorCS", {"start": v(-68.08, -66.16) * mm, "end": v(-37.84, -35.91) * mm});
            skLineSegment(sketch, "E246.MirrorCS", {"start": v(-37.84, -35.91) * mm, "end": v(-35.71, -38.03) * mm});
            skLineSegment(sketch, "E247", {"start": v(35.84, 38.26) * mm, "end": v(65.91, 68.33) * mm});
            skLineSegment(sketch, "E248", {"start": v(65.91, 68.33) * mm, "end": v(68.04, 66.2) * mm});
            skLineSegment(sketch, "E249", {"start": v(68.04, 66.2) * mm, "end": v(37.97, 36.14) * mm});
            skLineSegment(sketch, "E250", {"start": v(37.97, 36.14) * mm, "end": v(35.84, 38.26) * mm});
            skLineSegment(sketch, "E251.MirrorCS", {"start": v(35.84, -38.26) * mm, "end": v(65.91, -68.33) * mm});
            skLineSegment(sketch, "E252.MirrorCS", {"start": v(68.04, -66.2) * mm, "end": v(37.97, -36.14) * mm});
            skLineSegment(sketch, "E253.MirrorCS", {"start": v(37.97, -36.14) * mm, "end": v(35.84, -38.26) * mm});
            skLineSegment(sketch, "E254.MirrorCS", {"start": v(65.91, -68.33) * mm, "end": v(68.04, -66.2) * mm});
            skSolve(sketch);
        }
        {
            var Q0;
            Q0=makeQuery(id+"F2.opExtrude","CAP_FACE",FACE,{"disambiguationData":[OSD([sQuery(id+"F1.wireOp",EDGE,"E127"),sQuery(id+"F1.wireOp",EDGE,"E128"),sQuery(id+"F1.wireOp",EDGE,"E129"),sQuery(id+"F1.wireOp",EDGE,"E130"),sQuery(id+"F1.wireOp",EDGE,"E131"),sQuery(id+"F1.wireOp",EDGE,"E132"),sQuery(id+"F1.wireOp",EDGE,"E133"),sQuery(id+"F1.wireOp",EDGE,"E134"),sQuery(id+"F1.wireOp",EDGE,"E135"),sQuery(id+"F1.wireOp",EDGE,"E136"),sQuery(id+"F1.wireOp",EDGE,"E137"),sQuery(id+"F1.wireOp",EDGE,"E138"),sQuery(id+"F1.wireOp",EDGE,"E139"),sQuery(id+"F1.wireOp",EDGE,"E140"),sQuery(id+"F1.wireOp",EDGE,"E141"),sQuery(id+"F1.wireOp",EDGE,"E142"),sQuery(id+"F1.wireOp",EDGE,"E143"),sQuery(id+"F1.wireOp",EDGE,"E144"),sQuery(id+"F1.wireOp",EDGE,"E145"),sQuery(id+"F1.wireOp",EDGE,"E146"),sQuery(id+"F1.wireOp",EDGE,"E147"),sQuery(id+"F1.wireOp",EDGE,"E148"),sQuery(id+"F1.wireOp",EDGE,"E149"),sQuery(id+"F1.wireOp",EDGE,"E150"),sQuery(id+"F1.wireOp",EDGE,"E151"),sQuery(id+"F1.wireOp",EDGE,"E152"),sQuery(id+"F1.wireOp",EDGE,"E153"),sQuery(id+"F1.wireOp",EDGE,"E154"),sQuery(id+"F1.wireOp",EDGE,"E155"),sQuery(id+"F1.wireOp",EDGE,"E156"),sQuery(id+"F1.wireOp",EDGE,"E157"),sQuery(id+"F1.wireOp",EDGE,"E158"),sQuery(id+"F1.wireOp",EDGE,"E159"),sQuery(id+"F1.wireOp",EDGE,"E160"),sQuery(id+"F1.wireOp",EDGE,"E161"),sQuery(id+"F1.wireOp",EDGE,"E162"),sQuery(id+"F1.wireOp",EDGE,"E163"),sQuery(id+"F1.wireOp",EDGE,"E164"),sQuery(id+"F1.wireOp",EDGE,"E165"),sQuery(id+"F1.wireOp",EDGE,"E166"),sQuery(id+"F1.wireOp",EDGE,"E167"),sQuery(id+"F1.wireOp",EDGE,"E168"),sQuery(id+"F1.wireOp",EDGE,"E169"),sQuery(id+"F1.wireOp",EDGE,"E170"),sQuery(id+"F1.wireOp",EDGE,"E171"),sQuery(id+"F1.wireOp",EDGE,"E172"),sQuery(id+"F1.wireOp",EDGE,"E173"),sQuery(id+"F1.wireOp",EDGE,"E174"),sQuery(id+"F1.wireOp",EDGE,"E175"),sQuery(id+"F1.wireOp",EDGE,"E182"),sQuery(id+"F1.wireOp",EDGE,"E183"),sQuery(id+"F1.wireOp",EDGE,"E184"),sQuery(id+"F1.wireOp",EDGE,"E185"),sQuery(id+"F1.wireOp",EDGE,"E186"),sQuery(id+"F1.wireOp",EDGE,"E187"),sQuery(id+"F1.wireOp",EDGE,"E188"),sQuery(id+"F1.wireOp",EDGE,"E189"),sQuery(id+"F1.wireOp",EDGE,"E190"),sQuery(id+"F1.wireOp",EDGE,"E191"),sQuery(id+"F1.wireOp",EDGE,"E192"),sQuery(id+"F1.wireOp",EDGE,"E193"),sQuery(id+"F1.wireOp",EDGE,"E194"),sQuery(id+"F1.wireOp",EDGE,"E195"),sQuery(id+"F1.wireOp",EDGE,"E196"),sQuery(id+"F1.wireOp",EDGE,"E197"),sQuery(id+"F1.wireOp",EDGE,"E198"),sQuery(id+"F1.wireOp",EDGE,"E205"),sQuery(id+"F1.wireOp",EDGE,"E206"),sQuery(id+"F1.wireOp",EDGE,"E207"),sQuery(id+"F1.wireOp",EDGE,"E208"),sQuery(id+"F1.wireOp",EDGE,"E209"),sQuery(id+"F1.wireOp",EDGE,"E210"),sQuery(id+"F1.wireOp",EDGE,"E211"),sQuery(id+"F1.wireOp",EDGE,"E212"),sQuery(id+"F1.wireOp",EDGE,"E213"),sQuery(id+"F1.wireOp",EDGE,"E214"),sQuery(id+"F1.wireOp",EDGE,"E215"),sQuery(id+"F1.wireOp",EDGE,"E216"),sQuery(id+"F1.wireOp",EDGE,"E217"),sQuery(id+"F1.wireOp",EDGE,"E218"),sQuery(id+"F1.wireOp",EDGE,"E219"),sQuery(id+"F1.wireOp",EDGE,"E220"),sQuery(id+"F1.wireOp",EDGE,"E221"),sQuery(id+"F1.wireOp",EDGE,"E222"),sQuery(id+"F1.wireOp",EDGE,"E223"),sQuery(id+"F1.wireOp",EDGE,"E224"),sQuery(id+"F1.wireOp",EDGE,"E225"),sQuery(id+"F1.wireOp",EDGE,"E226"),sQuery(id+"F1.wireOp",EDGE,"E227"),sQuery(id+"F1.wireOp",EDGE,"E228"),sQuery(id+"F1.wireOp",EDGE,"E229"),sQuery(id+"F1.wireOp",EDGE,"E230"),sQuery(id+"F1.wireOp",EDGE,"E231"),sQuery(id+"F1.wireOp",EDGE,"E232"),sQuery(id+"F1.wireOp",EDGE,"E233.0"),sQuery(id+"F1.wireOp",EDGE,"E233.1"),sQuery(id+"F1.wireOp",EDGE,"E233.2"),sQuery(id+"F1.wireOp",EDGE,"E234"),sQuery(id+"F1.wireOp",EDGE,"E235"),sQuery(id+"F1.wireOp",EDGE,"E238")])],"isStart":false});
            var sketch = newSketch(context, id + "F4", { "sketchPlane" : qUnion([Q0])});
            skFitSpline(sketch, "E255.0", {"points": [v(-87.66, 92.45) * mm, v(-84.97, 98.15) * mm, v(-81.69, 90.34) * mm, v(-74.8, 87.37) * mm, v(-73.54, 82.07) * mm, v(-69.14, 78.46) * mm, v(-68.59, 74.17) * mm, v(-67, 72.67) * mm]});
            skArc(sketch, "E255.1", {"start": v(-92.45, 87.66) * mm, "mid": v(-89.64, 89.64) * mm, "end": v(-87.66, 92.45) * mm});
            skFitSpline(sketch, "E255.2", {"points": [v(-72.67, 67) * mm, v(-74.17, 68.59) * mm, v(-78.46, 69.14) * mm, v(-82.07, 73.54) * mm, v(-87.37, 74.8) * mm, v(-90.34, 81.69) * mm, v(-98.15, 84.97) * mm, v(-92.45, 87.66) * mm]});
            skLineSegment(sketch, "E255.3", {"start": v(-43.63, 36.56) * mm, "end": v(-72.67, 67) * mm});
            skLineSegment(sketch, "E255.4", {"start": v(-67, 72.67) * mm, "end": v(-36.56, 43.63) * mm});
            skLineSegment(sketch, "E255.5", {"start": v(-72.67, -67) * mm, "end": v(-43.63, -36.56) * mm});
            skFitSpline(sketch, "E255.6", {"points": [v(-92.45, -87.66) * mm, v(-98.15, -84.97) * mm, v(-90.34, -81.69) * mm, v(-87.37, -74.8) * mm, v(-82.07, -73.54) * mm, v(-78.46, -69.14) * mm, v(-74.17, -68.59) * mm, v(-72.67, -67) * mm]});
            skArc(sketch, "E255.7", {"start": v(-87.66, -92.45) * mm, "mid": v(-89.64, -89.64) * mm, "end": v(-92.45, -87.66) * mm});
            skFitSpline(sketch, "E255.8", {"points": [v(-67, -72.67) * mm, v(-68.59, -74.17) * mm, v(-69.14, -78.46) * mm, v(-73.54, -82.07) * mm, v(-74.8, -87.37) * mm, v(-81.69, -90.34) * mm, v(-84.97, -98.15) * mm, v(-87.66, -92.45) * mm]});
            skLineSegment(sketch, "E255.9", {"start": v(-36.56, -43.63) * mm, "end": v(-67, -72.67) * mm});
            skLineSegment(sketch, "E255.10", {"start": v(67, -72.67) * mm, "end": v(36.56, -43.63) * mm});
            skLineSegment(sketch, "E255.11", {"start": v(43.63, -36.56) * mm, "end": v(72.67, -67) * mm});
            skFitSpline(sketch, "E255.12", {"points": [v(72.67, -67) * mm, v(74.17, -68.59) * mm, v(78.46, -69.14) * mm, v(82.07, -73.54) * mm, v(87.37, -74.8) * mm, v(90.34, -81.69) * mm, v(98.15, -84.97) * mm, v(92.45, -87.66) * mm]});
            skFitSpline(sketch, "E255.13", {"points": [v(87.66, -92.45) * mm, v(84.97, -98.15) * mm, v(81.69, -90.34) * mm, v(74.8, -87.37) * mm, v(73.54, -82.07) * mm, v(69.14, -78.46) * mm, v(68.59, -74.17) * mm, v(67, -72.67) * mm]});
            skArc(sketch, "E255.14", {"start": v(92.45, -87.66) * mm, "mid": v(89.64, -89.64) * mm, "end": v(87.66, -92.45) * mm});
            skLineSegment(sketch, "E255.15", {"start": v(36.56, 43.63) * mm, "end": v(67, 72.67) * mm});
            skLineSegment(sketch, "E255.16", {"start": v(72.67, 67) * mm, "end": v(43.63, 36.56) * mm});
            skFitSpline(sketch, "E255.17", {"points": [v(67, 72.67) * mm, v(68.59, 74.17) * mm, v(69.14, 78.46) * mm, v(73.54, 82.07) * mm, v(74.8, 87.37) * mm, v(81.69, 90.34) * mm, v(84.97, 98.15) * mm, v(87.66, 92.45) * mm]});
            skFitSpline(sketch, "E255.18", {"points": [v(92.45, 87.66) * mm, v(98.15, 84.97) * mm, v(90.34, 81.69) * mm, v(87.37, 74.8) * mm, v(82.07, 73.54) * mm, v(78.46, 69.14) * mm, v(74.17, 68.59) * mm, v(72.67, 67) * mm]});
            skArc(sketch, "E255.19", {"start": v(87.66, 92.45) * mm, "mid": v(89.64, 89.64) * mm, "end": v(92.45, 87.66) * mm});
            skLineSegment(sketch, "E256.0", {"start": v(-67.84, 71.8) * mm, "end": v(-37.39, 42.76) * mm});
            skLineSegment(sketch, "E256.1", {"start": v(-42.76, 37.39) * mm, "end": v(-71.8, 67.84) * mm});
            skFitSpline(sketch, "E256.2", {"points": [v(-71.8, 67.84) * mm, v(-72.12, 68.17) * mm, v(-72.8, 68.75) * mm, v(-73.88, 69.36) * mm, v(-74.95, 69.82) * mm, v(-75.8, 70.14) * mm, v(-76.42, 70.38) * mm, v(-76.87, 70.57) * mm, v(-77.28, 70.76) * mm, v(-77.67, 70.97) * mm, v(-78.05, 71.22) * mm, v(-78.56, 71.58) * mm, v(-79.2, 72.1) * mm, v(-80.02, 72.78) * mm, v(-80.74, 73.36) * mm, v(-81.36, 73.82) * mm, v(-81.86, 74.15) * mm, v(-82.3, 74.4) * mm, v(-82.67, 74.6) * mm, v(-83.03, 74.77) * mm, v(-83.48, 74.96) * mm, v(-84.17, 75.24) * mm, v(-84.8, 75.5) * mm, v(-85.35, 75.75) * mm, v(-85.65, 75.92) * mm, v(-85.86, 76.06) * mm, v(-86.06, 76.2) * mm, v(-86.3, 76.41) * mm, v(-86.57, 76.7) * mm, v(-86.94, 77.16) * mm, v(-87.4, 77.82) * mm, v(-87.9, 78.59) * mm, v(-88.34, 79.23) * mm, v(-88.7, 79.73) * mm, v(-89.11, 80.22) * mm, v(-89.53, 80.69) * mm, v(-89.97, 81.13) * mm, v(-90.55, 81.7) * mm, v(-91.28, 82.37) * mm, v(-92.1, 83.11) * mm, v(-92.82, 83.8) * mm, v(-93.36, 84.4) * mm, v(-93.62, 84.81) * mm, v(-93.7, 85.04) * mm, v(-93.73, 85.14) * mm, v(-93.73, 85.2) * mm, v(-93.71, 85.26) * mm, v(-93.67, 85.36) * mm, v(-93.52, 85.57) * mm, v(-93.07, 85.97) * mm, v(-92.37, 86.37) * mm, v(-91.94, 86.57) * mm]});
            skArc(sketch, "E256.3", {"start": v(-91.94, 86.57) * mm, "mid": v(-88.79, 88.79) * mm, "end": v(-86.57, 91.94) * mm});
            skFitSpline(sketch, "E256.4", {"points": [v(-86.57, 91.94) * mm, v(-86.37, 92.37) * mm, v(-85.97, 93.07) * mm, v(-85.57, 93.52) * mm, v(-85.36, 93.67) * mm, v(-85.26, 93.71) * mm, v(-85.2, 93.73) * mm, v(-85.14, 93.73) * mm, v(-85.04, 93.7) * mm, v(-84.81, 93.62) * mm, v(-84.4, 93.36) * mm, v(-83.8, 92.82) * mm, v(-83.11, 92.1) * mm, v(-82.37, 91.28) * mm, v(-81.7, 90.55) * mm, v(-81.13, 89.97) * mm, v(-80.69, 89.53) * mm, v(-80.22, 89.11) * mm, v(-79.73, 88.7) * mm, v(-79.23, 88.34) * mm, v(-78.59, 87.9) * mm, v(-77.82, 87.4) * mm, v(-77.16, 86.94) * mm, v(-76.7, 86.57) * mm, v(-76.41, 86.3) * mm, v(-76.2, 86.06) * mm, v(-76.06, 85.86) * mm, v(-75.92, 85.65) * mm, v(-75.75, 85.35) * mm, v(-75.5, 84.8) * mm, v(-75.24, 84.17) * mm, v(-74.96, 83.48) * mm, v(-74.77, 83.03) * mm, v(-74.6, 82.67) * mm, v(-74.4, 82.3) * mm, v(-74.15, 81.86) * mm, v(-73.82, 81.36) * mm, v(-73.36, 80.74) * mm, v(-72.78, 80.02) * mm, v(-72.1, 79.2) * mm, v(-71.58, 78.56) * mm, v(-71.22, 78.05) * mm, v(-70.97, 77.67) * mm, v(-70.76, 77.28) * mm, v(-70.57, 76.87) * mm, v(-70.38, 76.42) * mm, v(-70.14, 75.8) * mm, v(-69.82, 74.95) * mm, v(-69.36, 73.88) * mm, v(-68.75, 72.8) * mm, v(-68.17, 72.12) * mm, v(-67.84, 71.8) * mm]});
            skLineSegment(sketch, "E257", {"start": v(-37.39, 42.76) * mm, "end": v(-36.56, 43.63) * mm});
            skLineSegment(sketch, "E258", {"start": v(-42.76, 37.39) * mm, "end": v(-43.63, 36.56) * mm});
            skLineSegment(sketch, "E259.0", {"start": v(-71.8, -67.84) * mm, "end": v(-42.76, -37.39) * mm});
            skLineSegment(sketch, "E259.1", {"start": v(-37.39, -42.76) * mm, "end": v(-67.84, -71.8) * mm});
            skFitSpline(sketch, "E259.2", {"points": [v(-67.84, -71.8) * mm, v(-68.17, -72.12) * mm, v(-68.75, -72.8) * mm, v(-69.36, -73.88) * mm, v(-69.82, -74.95) * mm, v(-70.14, -75.8) * mm, v(-70.38, -76.42) * mm, v(-70.57, -76.87) * mm, v(-70.76, -77.28) * mm, v(-70.97, -77.67) * mm, v(-71.22, -78.05) * mm, v(-71.58, -78.56) * mm, v(-72.1, -79.2) * mm, v(-72.78, -80.02) * mm, v(-73.36, -80.74) * mm, v(-73.82, -81.36) * mm, v(-74.15, -81.86) * mm, v(-74.4, -82.3) * mm, v(-74.6, -82.67) * mm, v(-74.77, -83.03) * mm, v(-74.96, -83.48) * mm, v(-75.24, -84.17) * mm, v(-75.5, -84.8) * mm, v(-75.75, -85.35) * mm, v(-75.92, -85.65) * mm, v(-76.06, -85.86) * mm, v(-76.2, -86.06) * mm, v(-76.41, -86.3) * mm, v(-76.7, -86.57) * mm, v(-77.16, -86.94) * mm, v(-77.82, -87.4) * mm, v(-78.59, -87.9) * mm, v(-79.23, -88.34) * mm, v(-79.73, -88.7) * mm, v(-80.22, -89.11) * mm, v(-80.69, -89.53) * mm, v(-81.13, -89.97) * mm, v(-81.7, -90.55) * mm, v(-82.37, -91.28) * mm, v(-83.11, -92.1) * mm, v(-83.8, -92.82) * mm, v(-84.4, -93.36) * mm, v(-84.81, -93.62) * mm, v(-85.04, -93.7) * mm, v(-85.14, -93.73) * mm, v(-85.2, -93.73) * mm, v(-85.26, -93.71) * mm, v(-85.36, -93.67) * mm, v(-85.57, -93.52) * mm, v(-85.97, -93.07) * mm, v(-86.37, -92.37) * mm, v(-86.57, -91.94) * mm]});
            skArc(sketch, "E259.3", {"start": v(-86.57, -91.94) * mm, "mid": v(-88.79, -88.79) * mm, "end": v(-91.94, -86.57) * mm});
            skFitSpline(sketch, "E259.4", {"points": [v(-91.94, -86.57) * mm, v(-92.37, -86.37) * mm, v(-93.07, -85.97) * mm, v(-93.52, -85.57) * mm, v(-93.67, -85.36) * mm, v(-93.71, -85.26) * mm, v(-93.73, -85.2) * mm, v(-93.73, -85.14) * mm, v(-93.7, -85.04) * mm, v(-93.62, -84.81) * mm, v(-93.36, -84.4) * mm, v(-92.82, -83.8) * mm, v(-92.1, -83.11) * mm, v(-91.28, -82.37) * mm, v(-90.55, -81.7) * mm, v(-89.97, -81.13) * mm, v(-89.53, -80.69) * mm, v(-89.11, -80.22) * mm, v(-88.7, -79.73) * mm, v(-88.34, -79.23) * mm, v(-87.9, -78.59) * mm, v(-87.4, -77.82) * mm, v(-86.94, -77.16) * mm, v(-86.57, -76.7) * mm, v(-86.3, -76.41) * mm, v(-86.06, -76.2) * mm, v(-85.86, -76.06) * mm, v(-85.65, -75.92) * mm, v(-85.35, -75.75) * mm, v(-84.8, -75.5) * mm, v(-84.17, -75.24) * mm, v(-83.48, -74.96) * mm, v(-83.03, -74.77) * mm, v(-82.67, -74.6) * mm, v(-82.3, -74.4) * mm, v(-81.86, -74.15) * mm, v(-81.36, -73.82) * mm, v(-80.74, -73.36) * mm, v(-80.02, -72.78) * mm, v(-79.2, -72.1) * mm, v(-78.56, -71.58) * mm, v(-78.05, -71.22) * mm, v(-77.67, -70.97) * mm, v(-77.28, -70.76) * mm, v(-76.87, -70.57) * mm, v(-76.42, -70.38) * mm, v(-75.8, -70.14) * mm, v(-74.95, -69.82) * mm, v(-73.88, -69.36) * mm, v(-72.8, -68.75) * mm, v(-72.12, -68.17) * mm, v(-71.8, -67.84) * mm]});
            skLineSegment(sketch, "E260", {"start": v(-42.76, -37.39) * mm, "end": v(-43.63, -36.56) * mm});
            skLineSegment(sketch, "E261", {"start": v(-36.56, -43.63) * mm, "end": v(-37.39, -42.76) * mm});
            skLineSegment(sketch, "E262.0", {"start": v(67.84, -71.8) * mm, "end": v(37.39, -42.76) * mm});
            skLineSegment(sketch, "E262.1", {"start": v(42.76, -37.39) * mm, "end": v(71.8, -67.84) * mm});
            skFitSpline(sketch, "E262.2", {"points": [v(71.8, -67.84) * mm, v(72.12, -68.17) * mm, v(72.8, -68.75) * mm, v(73.88, -69.36) * mm, v(74.95, -69.82) * mm, v(75.8, -70.14) * mm, v(76.42, -70.38) * mm, v(76.87, -70.57) * mm, v(77.28, -70.76) * mm, v(77.67, -70.97) * mm, v(78.05, -71.22) * mm, v(78.56, -71.58) * mm, v(79.2, -72.1) * mm, v(80.02, -72.78) * mm, v(80.74, -73.36) * mm, v(81.36, -73.82) * mm, v(81.86, -74.15) * mm, v(82.3, -74.4) * mm, v(82.67, -74.6) * mm, v(83.03, -74.77) * mm, v(83.48, -74.96) * mm, v(84.17, -75.24) * mm, v(84.8, -75.5) * mm, v(85.35, -75.75) * mm, v(85.65, -75.92) * mm, v(85.86, -76.06) * mm, v(86.06, -76.2) * mm, v(86.3, -76.41) * mm, v(86.57, -76.7) * mm, v(86.94, -77.16) * mm, v(87.4, -77.82) * mm, v(87.9, -78.59) * mm, v(88.34, -79.23) * mm, v(88.7, -79.73) * mm, v(89.11, -80.22) * mm, v(89.53, -80.69) * mm, v(89.97, -81.13) * mm, v(90.55, -81.7) * mm, v(91.28, -82.37) * mm, v(92.1, -83.11) * mm, v(92.82, -83.8) * mm, v(93.36, -84.4) * mm, v(93.62, -84.81) * mm, v(93.7, -85.04) * mm, v(93.73, -85.14) * mm, v(93.73, -85.2) * mm, v(93.71, -85.26) * mm, v(93.67, -85.36) * mm, v(93.52, -85.57) * mm, v(93.07, -85.97) * mm, v(92.37, -86.37) * mm, v(91.94, -86.57) * mm]});
            skArc(sketch, "E262.3", {"start": v(91.94, -86.57) * mm, "mid": v(88.79, -88.79) * mm, "end": v(86.57, -91.94) * mm});
            skFitSpline(sketch, "E262.4", {"points": [v(86.57, -91.94) * mm, v(86.37, -92.37) * mm, v(85.97, -93.07) * mm, v(85.57, -93.52) * mm, v(85.36, -93.67) * mm, v(85.26, -93.71) * mm, v(85.2, -93.73) * mm, v(85.14, -93.73) * mm, v(85.04, -93.7) * mm, v(84.81, -93.62) * mm, v(84.4, -93.36) * mm, v(83.8, -92.82) * mm, v(83.11, -92.1) * mm, v(82.37, -91.28) * mm, v(81.7, -90.55) * mm, v(81.13, -89.97) * mm, v(80.69, -89.53) * mm, v(80.22, -89.11) * mm, v(79.73, -88.7) * mm, v(79.23, -88.34) * mm, v(78.59, -87.9) * mm, v(77.82, -87.4) * mm, v(77.16, -86.94) * mm, v(76.7, -86.57) * mm, v(76.41, -86.3) * mm, v(76.2, -86.06) * mm, v(76.06, -85.86) * mm, v(75.92, -85.65) * mm, v(75.75, -85.35) * mm, v(75.5, -84.8) * mm, v(75.24, -84.17) * mm, v(74.96, -83.48) * mm, v(74.77, -83.03) * mm, v(74.6, -82.67) * mm, v(74.4, -82.3) * mm, v(74.15, -81.86) * mm, v(73.82, -81.36) * mm, v(73.36, -80.74) * mm, v(72.78, -80.02) * mm, v(72.1, -79.2) * mm, v(71.58, -78.56) * mm, v(71.22, -78.05) * mm, v(70.97, -77.67) * mm, v(70.76, -77.28) * mm, v(70.57, -76.87) * mm, v(70.38, -76.42) * mm, v(70.14, -75.8) * mm, v(69.82, -74.95) * mm, v(69.36, -73.88) * mm, v(68.75, -72.8) * mm, v(68.17, -72.12) * mm, v(67.84, -71.8) * mm]});
            skLineSegment(sketch, "E263", {"start": v(37.39, -42.76) * mm, "end": v(36.56, -43.63) * mm});
            skLineSegment(sketch, "E264", {"start": v(42.76, -37.39) * mm, "end": v(43.63, -36.56) * mm});
            skLineSegment(sketch, "E265.0", {"start": v(71.8, 67.84) * mm, "end": v(42.76, 37.39) * mm});
            skLineSegment(sketch, "E265.1", {"start": v(37.39, 42.76) * mm, "end": v(67.84, 71.8) * mm});
            skFitSpline(sketch, "E265.2", {"points": [v(67.84, 71.8) * mm, v(68.17, 72.12) * mm, v(68.75, 72.8) * mm, v(69.36, 73.88) * mm, v(69.82, 74.95) * mm, v(70.14, 75.8) * mm, v(70.38, 76.42) * mm, v(70.57, 76.87) * mm, v(70.76, 77.28) * mm, v(70.97, 77.67) * mm, v(71.22, 78.05) * mm, v(71.58, 78.56) * mm, v(72.1, 79.2) * mm, v(72.78, 80.02) * mm, v(73.36, 80.74) * mm, v(73.82, 81.36) * mm, v(74.15, 81.86) * mm, v(74.4, 82.3) * mm, v(74.6, 82.67) * mm, v(74.77, 83.03) * mm, v(74.96, 83.48) * mm, v(75.24, 84.17) * mm, v(75.5, 84.8) * mm, v(75.75, 85.35) * mm, v(75.92, 85.65) * mm, v(76.06, 85.86) * mm, v(76.2, 86.06) * mm, v(76.41, 86.3) * mm, v(76.7, 86.57) * mm, v(77.16, 86.94) * mm, v(77.82, 87.4) * mm, v(78.59, 87.9) * mm, v(79.23, 88.34) * mm, v(79.73, 88.7) * mm, v(80.22, 89.11) * mm, v(80.69, 89.53) * mm, v(81.13, 89.97) * mm, v(81.7, 90.55) * mm, v(82.37, 91.28) * mm, v(83.11, 92.1) * mm, v(83.8, 92.82) * mm, v(84.4, 93.36) * mm, v(84.81, 93.62) * mm, v(85.04, 93.7) * mm, v(85.14, 93.73) * mm, v(85.2, 93.73) * mm, v(85.26, 93.71) * mm, v(85.36, 93.67) * mm, v(85.57, 93.52) * mm, v(85.97, 93.07) * mm, v(86.37, 92.37) * mm, v(86.57, 91.94) * mm]});
            skArc(sketch, "E265.3", {"start": v(86.57, 91.94) * mm, "mid": v(88.79, 88.79) * mm, "end": v(91.94, 86.57) * mm});
            skFitSpline(sketch, "E265.4", {"points": [v(91.94, 86.57) * mm, v(92.37, 86.37) * mm, v(93.07, 85.97) * mm, v(93.52, 85.57) * mm, v(93.67, 85.36) * mm, v(93.71, 85.26) * mm, v(93.73, 85.2) * mm, v(93.73, 85.14) * mm, v(93.7, 85.04) * mm, v(93.62, 84.81) * mm, v(93.36, 84.4) * mm, v(92.82, 83.8) * mm, v(92.1, 83.11) * mm, v(91.28, 82.37) * mm, v(90.55, 81.7) * mm, v(89.97, 81.13) * mm, v(89.53, 80.69) * mm, v(89.11, 80.22) * mm, v(88.7, 79.73) * mm, v(88.34, 79.23) * mm, v(87.9, 78.59) * mm, v(87.4, 77.82) * mm, v(86.94, 77.16) * mm, v(86.57, 76.7) * mm, v(86.3, 76.41) * mm, v(86.06, 76.2) * mm, v(85.86, 76.06) * mm, v(85.65, 75.92) * mm, v(85.35, 75.75) * mm, v(84.8, 75.5) * mm, v(84.17, 75.24) * mm, v(83.48, 74.96) * mm, v(83.03, 74.77) * mm, v(82.67, 74.6) * mm, v(82.3, 74.4) * mm, v(81.86, 74.15) * mm, v(81.36, 73.82) * mm, v(80.74, 73.36) * mm, v(80.02, 72.78) * mm, v(79.2, 72.1) * mm, v(78.56, 71.58) * mm, v(78.05, 71.22) * mm, v(77.67, 70.97) * mm, v(77.28, 70.76) * mm, v(76.87, 70.57) * mm, v(76.42, 70.38) * mm, v(75.8, 70.14) * mm, v(74.95, 69.82) * mm, v(73.88, 69.36) * mm, v(72.8, 68.75) * mm, v(72.12, 68.17) * mm, v(71.8, 67.84) * mm]});
            skLineSegment(sketch, "E266", {"start": v(37.39, 42.76) * mm, "end": v(36.56, 43.63) * mm});
            skLineSegment(sketch, "E267", {"start": v(42.76, 37.39) * mm, "end": v(43.63, 36.56) * mm});
            skSolve(sketch);
        }
        {
            var Q0;
            Q0=makeQuery(id+"F3.imprint","IMPRINT",FACE,{"disambiguationData":[TD([[makeQuery(id+"F3.imprint","IMPRINT",EDGE,{"derivedFrom":sQuery(id+"F3.wireOp",EDGE,"E239")}),-1.0]])]});
            var sketch = newSketch(context, id + "F5", { "sketchPlane" : qUnion([Q0])});
            skFitSpline(sketch, "E268.0", {"points": [v(-87.66, 92.45) * mm, v(-84.97, 98.15) * mm, v(-81.69, 90.34) * mm, v(-74.8, 87.37) * mm, v(-73.54, 82.07) * mm, v(-69.14, 78.46) * mm, v(-68.59, 74.17) * mm, v(-67, 72.67) * mm]});
            skArc(sketch, "E268.1", {"start": v(-92.45, 87.66) * mm, "mid": v(-89.64, 89.64) * mm, "end": v(-87.66, 92.45) * mm});
            skFitSpline(sketch, "E268.2", {"points": [v(-72.67, 67) * mm, v(-74.17, 68.59) * mm, v(-78.46, 69.14) * mm, v(-82.07, 73.54) * mm, v(-87.37, 74.8) * mm, v(-90.34, 81.69) * mm, v(-98.15, 84.97) * mm, v(-92.45, 87.66) * mm]});
            skLineSegment(sketch, "E268.3", {"start": v(-43.63, 36.56) * mm, "end": v(-72.67, 67) * mm});
            skLineSegment(sketch, "E268.4", {"start": v(-67, 72.67) * mm, "end": v(-36.56, 43.63) * mm});
            skFitSpline(sketch, "E268.5", {"points": [v(-36.56, 43.63) * mm, v(-33.38, 40.6) * mm, v(-28.3, 41.37) * mm, v(-16.78, 37.85) * mm, v(-16.12, 22.42) * mm, v(3.25, 19.6) * mm, v(21.88, 24.54) * mm, v(32.38, 39.64) * mm, v(36.56, 43.63) * mm]});
            skLineSegment(sketch, "E268.6", {"start": v(36.56, 43.63) * mm, "end": v(67, 72.67) * mm});
            skFitSpline(sketch, "E268.7", {"points": [v(67, 72.67) * mm, v(68.59, 74.17) * mm, v(69.14, 78.46) * mm, v(73.54, 82.07) * mm, v(74.8, 87.37) * mm, v(81.69, 90.34) * mm, v(84.97, 98.15) * mm, v(87.66, 92.45) * mm]});
            skArc(sketch, "E268.8", {"start": v(87.66, 92.45) * mm, "mid": v(89.64, 89.64) * mm, "end": v(92.45, 87.66) * mm});
            skFitSpline(sketch, "E268.9", {"points": [v(92.45, 87.66) * mm, v(98.15, 84.97) * mm, v(90.34, 81.69) * mm, v(87.37, 74.8) * mm, v(82.07, 73.54) * mm, v(78.46, 69.14) * mm, v(74.17, 68.59) * mm, v(72.67, 67) * mm]});
            skLineSegment(sketch, "E268.10", {"start": v(72.67, 67) * mm, "end": v(43.63, 36.56) * mm});
            skFitSpline(sketch, "E268.11", {"points": [v(43.63, 36.56) * mm, v(40.74, 33.53) * mm, v(40, 27.02) * mm, v(47.4, 4.5) * mm, v(77.6, 23.46) * mm, v(77.6, 0) * mm]});
            skFitSpline(sketch, "E268.12", {"points": [v(77.6, 0) * mm, v(77.6, -23.46) * mm, v(47.4, -4.5) * mm, v(40, -27.02) * mm, v(40.74, -33.53) * mm, v(43.63, -36.56) * mm]});
            skLineSegment(sketch, "E268.13", {"start": v(43.63, -36.56) * mm, "end": v(72.67, -67) * mm});
            skFitSpline(sketch, "E268.14", {"points": [v(72.67, -67) * mm, v(74.17, -68.59) * mm, v(78.46, -69.14) * mm, v(82.07, -73.54) * mm, v(87.37, -74.8) * mm, v(90.34, -81.69) * mm, v(98.15, -84.97) * mm, v(92.45, -87.66) * mm]});
            skArc(sketch, "E268.15", {"start": v(92.45, -87.66) * mm, "mid": v(89.64, -89.64) * mm, "end": v(87.66, -92.45) * mm});
            skFitSpline(sketch, "E268.16", {"points": [v(87.66, -92.45) * mm, v(84.97, -98.15) * mm, v(81.69, -90.34) * mm, v(74.8, -87.37) * mm, v(73.54, -82.07) * mm, v(69.14, -78.46) * mm, v(68.59, -74.17) * mm, v(67, -72.67) * mm]});
            skLineSegment(sketch, "E268.17", {"start": v(67, -72.67) * mm, "end": v(36.56, -43.63) * mm});
            skFitSpline(sketch, "E268.18", {"points": [v(36.56, -43.63) * mm, v(32.38, -39.64) * mm, v(21.88, -24.54) * mm, v(3.25, -19.6) * mm, v(-16.12, -22.42) * mm, v(-16.78, -37.85) * mm, v(-28.3, -41.37) * mm, v(-33.38, -40.6) * mm, v(-36.56, -43.63) * mm]});
            skLineSegment(sketch, "E268.19", {"start": v(-36.56, -43.63) * mm, "end": v(-67, -72.67) * mm});
            skLineSegment(sketch, "E268.20", {"start": v(-72.67, -67) * mm, "end": v(-43.63, -36.56) * mm});
            skFitSpline(sketch, "E268.21", {"points": [v(-43.63, -36.56) * mm, v(-39.67, -32.4) * mm, v(-42.94, -27.6) * mm, v(-30.23, -18.41) * mm, v(-34.48, -8.7) * mm, v(-36.58, -4.27) * mm]});
            skFitSpline(sketch, "E268.22", {"points": [v(-36.58, 4.27) * mm, v(-34.48, 8.7) * mm, v(-30.23, 18.41) * mm, v(-42.94, 27.6) * mm, v(-39.67, 32.4) * mm, v(-43.63, 36.56) * mm]});
            skArc(sketch, "E268.23", {"start": v(-36.58, 4.27) * mm, "mid": v(-37.53, 0) * mm, "end": v(-36.58, -4.27) * mm});
            skFitSpline(sketch, "E268.24", {"points": [v(-67, -72.67) * mm, v(-68.59, -74.17) * mm, v(-69.14, -78.46) * mm, v(-73.54, -82.07) * mm, v(-74.8, -87.37) * mm, v(-81.69, -90.34) * mm, v(-84.97, -98.15) * mm, v(-87.66, -92.45) * mm]});
            skArc(sketch, "E268.25", {"start": v(-87.66, -92.45) * mm, "mid": v(-89.64, -89.64) * mm, "end": v(-92.45, -87.66) * mm});
            skFitSpline(sketch, "E268.26", {"points": [v(-92.45, -87.66) * mm, v(-98.15, -84.97) * mm, v(-90.34, -81.69) * mm, v(-87.37, -74.8) * mm, v(-82.07, -73.54) * mm, v(-78.46, -69.14) * mm, v(-74.17, -68.59) * mm, v(-72.67, -67) * mm]});
            skFitSpline(sketch, "E269.0", {"points": [v(-35.5, 3.76) * mm, v(-34.86, 5.1) * mm, v(-33.85, 7.3) * mm, v(-32.78, 10.4) * mm, v(-32.23, 12.8) * mm, v(-32.06, 14.82) * mm, v(-32.17, 16.44) * mm, v(-32.38, 17.65) * mm, v(-32.7, 18.65) * mm, v(-33.02, 19.43) * mm, v(-33.4, 20.18) * mm, v(-33.94, 21.08) * mm, v(-34.9, 22.44) * mm, v(-35.97, 23.7) * mm, v(-37, 24.89) * mm, v(-37.7, 25.73) * mm, v(-38.33, 26.54) * mm, v(-38.75, 27.16) * mm, v(-39, 27.63) * mm, v(-39.17, 27.96) * mm, v(-39.28, 28.27) * mm, v(-39.39, 28.65) * mm, v(-39.46, 29.18) * mm, v(-39.48, 29.95) * mm, v(-39.5, 30.87) * mm, v(-39.62, 31.94) * mm, v(-39.93, 33.15) * mm, v(-40.5, 34.45) * mm, v(-41.4, 35.85) * mm, v(-42.25, 36.86) * mm, v(-42.76, 37.39) * mm]});
            skArc(sketch, "E269.1", {"start": v(-35.5, 3.76) * mm, "mid": v(-36.33, 0) * mm, "end": v(-35.5, -3.76) * mm});
            skFitSpline(sketch, "E269.2", {"points": [v(-42.76, -37.39) * mm, v(-42.25, -36.86) * mm, v(-41.4, -35.85) * mm, v(-40.5, -34.45) * mm, v(-39.93, -33.15) * mm, v(-39.62, -31.94) * mm, v(-39.5, -30.87) * mm, v(-39.48, -29.95) * mm, v(-39.46, -29.18) * mm, v(-39.39, -28.65) * mm, v(-39.28, -28.27) * mm, v(-39.17, -27.96) * mm, v(-39, -27.63) * mm, v(-38.75, -27.16) * mm, v(-38.33, -26.54) * mm, v(-37.7, -25.73) * mm, v(-37, -24.89) * mm, v(-35.97, -23.7) * mm, v(-34.9, -22.44) * mm, v(-33.94, -21.08) * mm, v(-33.4, -20.18) * mm, v(-33.02, -19.43) * mm, v(-32.7, -18.65) * mm, v(-32.38, -17.65) * mm, v(-32.17, -16.44) * mm, v(-32.06, -14.82) * mm, v(-32.23, -12.8) * mm, v(-32.78, -10.4) * mm, v(-33.85, -7.3) * mm, v(-34.86, -5.1) * mm, v(-35.5, -3.76) * mm]});
            skLineSegment(sketch, "E269.3", {"start": v(-71.8, -67.84) * mm, "end": v(-42.76, -37.39) * mm});
            skLineSegment(sketch, "E269.4", {"start": v(71.8, 67.84) * mm, "end": v(42.76, 37.39) * mm});
            skFitSpline(sketch, "E269.5", {"points": [v(91.94, 86.57) * mm, v(92.37, 86.37) * mm, v(93.07, 85.97) * mm, v(93.52, 85.57) * mm, v(93.67, 85.36) * mm, v(93.71, 85.26) * mm, v(93.73, 85.2) * mm, v(93.73, 85.14) * mm, v(93.7, 85.04) * mm, v(93.62, 84.81) * mm, v(93.36, 84.4) * mm, v(92.82, 83.8) * mm, v(92.1, 83.11) * mm, v(91.28, 82.37) * mm, v(90.55, 81.7) * mm, v(89.97, 81.13) * mm, v(89.53, 80.69) * mm, v(89.11, 80.22) * mm, v(88.7, 79.73) * mm, v(88.34, 79.23) * mm, v(87.9, 78.59) * mm, v(87.4, 77.82) * mm, v(86.94, 77.16) * mm, v(86.57, 76.7) * mm, v(86.3, 76.41) * mm, v(86.06, 76.2) * mm, v(85.86, 76.06) * mm, v(85.65, 75.92) * mm, v(85.35, 75.75) * mm, v(84.8, 75.5) * mm, v(84.17, 75.24) * mm, v(83.48, 74.96) * mm, v(83.03, 74.77) * mm, v(82.67, 74.6) * mm, v(82.3, 74.4) * mm, v(81.86, 74.15) * mm, v(81.36, 73.82) * mm, v(80.74, 73.36) * mm, v(80.02, 72.78) * mm, v(79.2, 72.1) * mm, v(78.56, 71.58) * mm, v(78.05, 71.22) * mm, v(77.67, 70.97) * mm, v(77.28, 70.76) * mm, v(76.87, 70.57) * mm, v(76.42, 70.38) * mm, v(75.8, 70.14) * mm, v(74.95, 69.82) * mm, v(73.88, 69.36) * mm, v(72.8, 68.75) * mm, v(72.12, 68.17) * mm, v(71.8, 67.84) * mm]});
            skArc(sketch, "E269.6", {"start": v(86.57, 91.94) * mm, "mid": v(88.79, 88.79) * mm, "end": v(91.94, 86.57) * mm});
            skFitSpline(sketch, "E269.7", {"points": [v(67.84, 71.8) * mm, v(68.17, 72.12) * mm, v(68.75, 72.8) * mm, v(69.36, 73.88) * mm, v(69.82, 74.95) * mm, v(70.14, 75.8) * mm, v(70.38, 76.42) * mm, v(70.57, 76.87) * mm, v(70.76, 77.28) * mm, v(70.97, 77.67) * mm, v(71.22, 78.05) * mm, v(71.58, 78.56) * mm, v(72.1, 79.2) * mm, v(72.78, 80.02) * mm, v(73.36, 80.74) * mm, v(73.82, 81.36) * mm, v(74.15, 81.86) * mm, v(74.4, 82.3) * mm, v(74.6, 82.67) * mm, v(74.77, 83.03) * mm, v(74.96, 83.48) * mm, v(75.24, 84.17) * mm, v(75.5, 84.8) * mm, v(75.75, 85.35) * mm, v(75.92, 85.65) * mm, v(76.06, 85.86) * mm, v(76.2, 86.06) * mm, v(76.41, 86.3) * mm, v(76.7, 86.57) * mm, v(77.16, 86.94) * mm, v(77.82, 87.4) * mm, v(78.59, 87.9) * mm, v(79.23, 88.34) * mm, v(79.73, 88.7) * mm, v(80.22, 89.11) * mm, v(80.69, 89.53) * mm, v(81.13, 89.97) * mm, v(81.7, 90.55) * mm, v(82.37, 91.28) * mm, v(83.11, 92.1) * mm, v(83.8, 92.82) * mm, v(84.4, 93.36) * mm, v(84.81, 93.62) * mm, v(85.04, 93.7) * mm, v(85.14, 93.73) * mm, v(85.2, 93.73) * mm, v(85.26, 93.71) * mm, v(85.36, 93.67) * mm, v(85.57, 93.52) * mm, v(85.97, 93.07) * mm, v(86.37, 92.37) * mm, v(86.57, 91.94) * mm]});
            skLineSegment(sketch, "E269.8", {"start": v(37.39, 42.76) * mm, "end": v(67.84, 71.8) * mm});
            skFitSpline(sketch, "E269.9", {"points": [v(-37.39, 42.76) * mm, v(-36.88, 42.27) * mm, v(-35.85, 41.44) * mm, v(-34.32, 40.58) * mm, v(-32.81, 40.06) * mm, v(-31.36, 39.78) * mm, v(-29.97, 39.64) * mm, v(-28.85, 39.56) * mm, v(-27.97, 39.48) * mm, v(-27.1, 39.38) * mm, v(-25.99, 39.18) * mm, v(-24.67, 38.84) * mm, v(-23.4, 38.38) * mm, v(-22.24, 37.8) * mm, v(-21.22, 37.12) * mm, v(-20.38, 36.31) * mm, v(-19.65, 35.34) * mm, v(-19.02, 34.22) * mm, v(-18.27, 32.57) * mm, v(-17.61, 30.74) * mm, v(-16.93, 28.87) * mm, v(-16.36, 27.47) * mm, v(-15.7, 26.1) * mm, v(-15.04, 25.04) * mm, v(-14.41, 24.23) * mm, v(-13.72, 23.48) * mm, v(-12.76, 22.66) * mm, v(-11.48, 21.85) * mm, v(-9.64, 20.97) * mm, v(-7.15, 20.22) * mm, v(-3.98, 19.74) * mm, v(-0.77, 19.57) * mm, v(2.34, 19.62) * mm, v(5.36, 19.86) * mm, v(8.3, 20.33) * mm, v(11.16, 21.02) * mm, v(13.92, 21.95) * mm, v(16.6, 23.15) * mm, v(18.74, 24.36) * mm, v(20.4, 25.46) * mm, v(22.05, 26.66) * mm, v(24.02, 28.32) * mm, v(27.03, 31.2) * mm, v(30.52, 35.06) * mm, v(34.25, 39.46) * mm, v(36.41, 41.83) * mm, v(37.39, 42.76) * mm]});
            skFitSpline(sketch, "E269.10", {"points": [v(-71.8, 67.84) * mm, v(-72.12, 68.17) * mm, v(-72.8, 68.75) * mm, v(-73.88, 69.36) * mm, v(-74.95, 69.82) * mm, v(-75.8, 70.14) * mm, v(-76.42, 70.38) * mm, v(-76.87, 70.57) * mm, v(-77.28, 70.76) * mm, v(-77.67, 70.97) * mm, v(-78.05, 71.22) * mm, v(-78.56, 71.58) * mm, v(-79.2, 72.1) * mm, v(-80.02, 72.78) * mm, v(-80.74, 73.36) * mm, v(-81.36, 73.82) * mm, v(-81.86, 74.15) * mm, v(-82.3, 74.4) * mm, v(-82.67, 74.6) * mm, v(-83.03, 74.77) * mm, v(-83.48, 74.96) * mm, v(-84.17, 75.24) * mm, v(-84.8, 75.5) * mm, v(-85.35, 75.75) * mm, v(-85.65, 75.92) * mm, v(-85.86, 76.06) * mm, v(-86.06, 76.2) * mm, v(-86.3, 76.41) * mm, v(-86.57, 76.7) * mm, v(-86.94, 77.16) * mm, v(-87.4, 77.82) * mm, v(-87.9, 78.59) * mm, v(-88.34, 79.23) * mm, v(-88.7, 79.73) * mm, v(-89.11, 80.22) * mm, v(-89.53, 80.69) * mm, v(-89.97, 81.13) * mm, v(-90.55, 81.7) * mm, v(-91.28, 82.37) * mm, v(-92.1, 83.11) * mm, v(-92.82, 83.8) * mm, v(-93.36, 84.4) * mm, v(-93.62, 84.81) * mm, v(-93.7, 85.04) * mm, v(-93.73, 85.14) * mm, v(-93.73, 85.2) * mm, v(-93.71, 85.26) * mm, v(-93.67, 85.36) * mm, v(-93.52, 85.57) * mm, v(-93.07, 85.97) * mm, v(-92.37, 86.37) * mm, v(-91.94, 86.57) * mm]});
            skArc(sketch, "E269.11", {"start": v(-91.94, 86.57) * mm, "mid": v(-88.79, 88.79) * mm, "end": v(-86.57, 91.94) * mm});
            skFitSpline(sketch, "E269.12", {"points": [v(-86.57, 91.94) * mm, v(-86.37, 92.37) * mm, v(-85.97, 93.07) * mm, v(-85.57, 93.52) * mm, v(-85.36, 93.67) * mm, v(-85.26, 93.71) * mm, v(-85.2, 93.73) * mm, v(-85.14, 93.73) * mm, v(-85.04, 93.7) * mm, v(-84.81, 93.62) * mm, v(-84.4, 93.36) * mm, v(-83.8, 92.82) * mm, v(-83.11, 92.1) * mm, v(-82.37, 91.28) * mm, v(-81.7, 90.55) * mm, v(-81.13, 89.97) * mm, v(-80.69, 89.53) * mm, v(-80.22, 89.11) * mm, v(-79.73, 88.7) * mm, v(-79.23, 88.34) * mm, v(-78.59, 87.9) * mm, v(-77.82, 87.4) * mm, v(-77.16, 86.94) * mm, v(-76.7, 86.57) * mm, v(-76.41, 86.3) * mm, v(-76.2, 86.06) * mm, v(-76.06, 85.86) * mm, v(-75.92, 85.65) * mm, v(-75.75, 85.35) * mm, v(-75.5, 84.8) * mm, v(-75.24, 84.17) * mm, v(-74.96, 83.48) * mm, v(-74.77, 83.03) * mm, v(-74.6, 82.67) * mm, v(-74.4, 82.3) * mm, v(-74.15, 81.86) * mm, v(-73.82, 81.36) * mm, v(-73.36, 80.74) * mm, v(-72.78, 80.02) * mm, v(-72.1, 79.2) * mm, v(-71.58, 78.56) * mm, v(-71.22, 78.05) * mm, v(-70.97, 77.67) * mm, v(-70.76, 77.28) * mm, v(-70.57, 76.87) * mm, v(-70.38, 76.42) * mm, v(-70.14, 75.8) * mm, v(-69.82, 74.95) * mm, v(-69.36, 73.88) * mm, v(-68.75, 72.8) * mm, v(-68.17, 72.12) * mm, v(-67.84, 71.8) * mm]});
            skLineSegment(sketch, "E269.13", {"start": v(-67.84, 71.8) * mm, "end": v(-37.39, 42.76) * mm});
            skFitSpline(sketch, "E269.14", {"points": [v(42.76, 37.39) * mm, v(42.16, 36.76) * mm, v(41.14, 35.48) * mm, v(40.13, 33.49) * mm, v(39.58, 31.45) * mm, v(39.4, 29.41) * mm, v(39.49, 27.72) * mm, v(39.65, 26.36) * mm, v(39.87, 25) * mm, v(40.25, 23.27) * mm, v(40.9, 21.24) * mm, v(41.74, 19.32) * mm, v(42.63, 17.85) * mm, v(43.47, 16.8) * mm, v(44.17, 16.07) * mm, v(44.93, 15.43) * mm, v(46, 14.7) * mm, v(47.46, 13.99) * mm, v(49.32, 13.42) * mm, v(51.28, 13.07) * mm, v(53.97, 12.83) * mm, v(57.45, 12.83) * mm, v(61.63, 12.98) * mm, v(65.64, 12.96) * mm, v(68.63, 12.55) * mm, v(70.7, 11.87) * mm, v(72.1, 11.17) * mm, v(73.3, 10.23) * mm, v(74.33, 9.02) * mm, v(75.2, 7.46) * mm, v(76.1, 4.83) * mm, v(76.4, 2.15) * mm, v(76.4, 0) * mm]});
            skFitSpline(sketch, "E269.15", {"points": [v(76.4, 0) * mm, v(76.4, -2.15) * mm, v(76.1, -4.83) * mm, v(75.2, -7.46) * mm, v(74.33, -9.02) * mm, v(73.3, -10.23) * mm, v(72.1, -11.17) * mm, v(70.7, -11.87) * mm, v(68.63, -12.55) * mm, v(65.64, -12.96) * mm, v(61.63, -12.98) * mm, v(57.45, -12.83) * mm, v(53.97, -12.83) * mm, v(51.28, -13.07) * mm, v(49.32, -13.42) * mm, v(47.46, -13.99) * mm, v(46, -14.7) * mm, v(44.93, -15.43) * mm, v(44.17, -16.07) * mm, v(43.47, -16.8) * mm, v(42.63, -17.85) * mm, v(41.74, -19.32) * mm, v(40.9, -21.24) * mm, v(40.25, -23.27) * mm, v(39.87, -25) * mm, v(39.65, -26.36) * mm, v(39.49, -27.72) * mm, v(39.4, -29.41) * mm, v(39.58, -31.45) * mm, v(40.13, -33.49) * mm, v(41.14, -35.48) * mm, v(42.16, -36.76) * mm, v(42.76, -37.39) * mm]});
            skLineSegment(sketch, "E269.16", {"start": v(42.76, -37.39) * mm, "end": v(71.8, -67.84) * mm});
            skFitSpline(sketch, "E269.17", {"points": [v(71.8, -67.84) * mm, v(72.12, -68.17) * mm, v(72.8, -68.75) * mm, v(73.88, -69.36) * mm, v(74.95, -69.82) * mm, v(75.8, -70.14) * mm, v(76.42, -70.38) * mm, v(76.87, -70.57) * mm, v(77.28, -70.76) * mm, v(77.67, -70.97) * mm, v(78.05, -71.22) * mm, v(78.56, -71.58) * mm, v(79.2, -72.1) * mm, v(80.02, -72.78) * mm, v(80.74, -73.36) * mm, v(81.36, -73.82) * mm, v(81.86, -74.15) * mm, v(82.3, -74.4) * mm, v(82.67, -74.6) * mm, v(83.03, -74.77) * mm, v(83.48, -74.96) * mm, v(84.17, -75.24) * mm, v(84.8, -75.5) * mm, v(85.35, -75.75) * mm, v(85.65, -75.92) * mm, v(85.86, -76.06) * mm, v(86.06, -76.2) * mm, v(86.3, -76.41) * mm, v(86.57, -76.7) * mm, v(86.94, -77.16) * mm, v(87.4, -77.82) * mm, v(87.9, -78.59) * mm, v(88.34, -79.23) * mm, v(88.7, -79.73) * mm, v(89.11, -80.22) * mm, v(89.53, -80.69) * mm, v(89.97, -81.13) * mm, v(90.55, -81.7) * mm, v(91.28, -82.37) * mm, v(92.1, -83.11) * mm, v(92.82, -83.8) * mm, v(93.36, -84.4) * mm, v(93.62, -84.81) * mm, v(93.7, -85.04) * mm, v(93.73, -85.14) * mm, v(93.73, -85.2) * mm, v(93.71, -85.26) * mm, v(93.67, -85.36) * mm, v(93.52, -85.57) * mm, v(93.07, -85.97) * mm, v(92.37, -86.37) * mm, v(91.94, -86.57) * mm]});
            skLineSegment(sketch, "E269.18", {"start": v(-42.76, 37.39) * mm, "end": v(-71.8, 67.84) * mm});
            skArc(sketch, "E269.19", {"start": v(91.94, -86.57) * mm, "mid": v(88.79, -88.79) * mm, "end": v(86.57, -91.94) * mm});
            skFitSpline(sketch, "E269.20", {"points": [v(86.57, -91.94) * mm, v(86.37, -92.37) * mm, v(85.97, -93.07) * mm, v(85.57, -93.52) * mm, v(85.36, -93.67) * mm, v(85.26, -93.71) * mm, v(85.2, -93.73) * mm, v(85.14, -93.73) * mm, v(85.04, -93.7) * mm, v(84.81, -93.62) * mm, v(84.4, -93.36) * mm, v(83.8, -92.82) * mm, v(83.11, -92.1) * mm, v(82.37, -91.28) * mm, v(81.7, -90.55) * mm, v(81.13, -89.97) * mm, v(80.69, -89.53) * mm, v(80.22, -89.11) * mm, v(79.73, -88.7) * mm, v(79.23, -88.34) * mm, v(78.59, -87.9) * mm, v(77.82, -87.4) * mm, v(77.16, -86.94) * mm, v(76.7, -86.57) * mm, v(76.41, -86.3) * mm, v(76.2, -86.06) * mm, v(76.06, -85.86) * mm, v(75.92, -85.65) * mm, v(75.75, -85.35) * mm, v(75.5, -84.8) * mm, v(75.24, -84.17) * mm, v(74.96, -83.48) * mm, v(74.77, -83.03) * mm, v(74.6, -82.67) * mm, v(74.4, -82.3) * mm, v(74.15, -81.86) * mm, v(73.82, -81.36) * mm, v(73.36, -80.74) * mm, v(72.78, -80.02) * mm, v(72.1, -79.2) * mm, v(71.58, -78.56) * mm, v(71.22, -78.05) * mm, v(70.97, -77.67) * mm, v(70.76, -77.28) * mm, v(70.57, -76.87) * mm, v(70.38, -76.42) * mm, v(70.14, -75.8) * mm, v(69.82, -74.95) * mm, v(69.36, -73.88) * mm, v(68.75, -72.8) * mm, v(68.17, -72.12) * mm, v(67.84, -71.8) * mm]});
            skLineSegment(sketch, "E269.21", {"start": v(67.84, -71.8) * mm, "end": v(37.39, -42.76) * mm});
            skFitSpline(sketch, "E269.22", {"points": [v(37.39, -42.76) * mm, v(36.41, -41.83) * mm, v(34.25, -39.46) * mm, v(30.52, -35.06) * mm, v(27.03, -31.2) * mm, v(24.02, -28.32) * mm, v(22.05, -26.66) * mm, v(20.4, -25.46) * mm, v(18.74, -24.36) * mm, v(16.6, -23.15) * mm, v(13.92, -21.95) * mm, v(11.16, -21.02) * mm, v(8.3, -20.33) * mm, v(5.36, -19.86) * mm, v(2.34, -19.62) * mm, v(-0.77, -19.57) * mm, v(-3.98, -19.74) * mm, v(-7.15, -20.22) * mm, v(-9.64, -20.97) * mm, v(-11.48, -21.85) * mm, v(-12.76, -22.66) * mm, v(-13.72, -23.48) * mm, v(-14.41, -24.23) * mm, v(-15.04, -25.04) * mm, v(-15.7, -26.1) * mm, v(-16.36, -27.47) * mm, v(-16.93, -28.87) * mm, v(-17.61, -30.74) * mm, v(-18.27, -32.57) * mm, v(-19.02, -34.22) * mm, v(-19.65, -35.34) * mm, v(-20.38, -36.31) * mm, v(-21.22, -37.12) * mm, v(-22.24, -37.8) * mm, v(-23.4, -38.38) * mm, v(-24.67, -38.84) * mm, v(-25.99, -39.18) * mm, v(-27.1, -39.38) * mm, v(-27.97, -39.48) * mm, v(-28.85, -39.56) * mm, v(-29.97, -39.64) * mm, v(-31.36, -39.78) * mm, v(-32.81, -40.06) * mm, v(-34.32, -40.58) * mm, v(-35.85, -41.44) * mm, v(-36.88, -42.27) * mm, v(-37.39, -42.76) * mm]});
            skLineSegment(sketch, "E269.23", {"start": v(-37.39, -42.76) * mm, "end": v(-67.84, -71.8) * mm});
            skFitSpline(sketch, "E269.24", {"points": [v(-67.84, -71.8) * mm, v(-68.17, -72.12) * mm, v(-68.75, -72.8) * mm, v(-69.36, -73.88) * mm, v(-69.82, -74.95) * mm, v(-70.14, -75.8) * mm, v(-70.38, -76.42) * mm, v(-70.57, -76.87) * mm, v(-70.76, -77.28) * mm, v(-70.97, -77.67) * mm, v(-71.22, -78.05) * mm, v(-71.58, -78.56) * mm, v(-72.1, -79.2) * mm, v(-72.78, -80.02) * mm, v(-73.36, -80.74) * mm, v(-73.82, -81.36) * mm, v(-74.15, -81.86) * mm, v(-74.4, -82.3) * mm, v(-74.6, -82.67) * mm, v(-74.77, -83.03) * mm, v(-74.96, -83.48) * mm, v(-75.24, -84.17) * mm, v(-75.5, -84.8) * mm, v(-75.75, -85.35) * mm, v(-75.92, -85.65) * mm, v(-76.06, -85.86) * mm, v(-76.2, -86.06) * mm, v(-76.41, -86.3) * mm, v(-76.7, -86.57) * mm, v(-77.16, -86.94) * mm, v(-77.82, -87.4) * mm, v(-78.59, -87.9) * mm, v(-79.23, -88.34) * mm, v(-79.73, -88.7) * mm, v(-80.22, -89.11) * mm, v(-80.69, -89.53) * mm, v(-81.13, -89.97) * mm, v(-81.7, -90.55) * mm, v(-82.37, -91.28) * mm, v(-83.11, -92.1) * mm, v(-83.8, -92.82) * mm, v(-84.4, -93.36) * mm, v(-84.81, -93.62) * mm, v(-85.04, -93.7) * mm, v(-85.14, -93.73) * mm, v(-85.2, -93.73) * mm, v(-85.26, -93.71) * mm, v(-85.36, -93.67) * mm, v(-85.57, -93.52) * mm, v(-85.97, -93.07) * mm, v(-86.37, -92.37) * mm, v(-86.57, -91.94) * mm]});
            skArc(sketch, "E269.25", {"start": v(-86.57, -91.94) * mm, "mid": v(-88.79, -88.79) * mm, "end": v(-91.94, -86.57) * mm});
            skFitSpline(sketch, "E269.26", {"points": [v(-91.94, -86.57) * mm, v(-92.37, -86.37) * mm, v(-93.07, -85.97) * mm, v(-93.52, -85.57) * mm, v(-93.67, -85.36) * mm, v(-93.71, -85.26) * mm, v(-93.73, -85.2) * mm, v(-93.73, -85.14) * mm, v(-93.7, -85.04) * mm, v(-93.62, -84.81) * mm, v(-93.36, -84.4) * mm, v(-92.82, -83.8) * mm, v(-92.1, -83.11) * mm, v(-91.28, -82.37) * mm, v(-90.55, -81.7) * mm, v(-89.97, -81.13) * mm, v(-89.53, -80.69) * mm, v(-89.11, -80.22) * mm, v(-88.7, -79.73) * mm, v(-88.34, -79.23) * mm, v(-87.9, -78.59) * mm, v(-87.4, -77.82) * mm, v(-86.94, -77.16) * mm, v(-86.57, -76.7) * mm, v(-86.3, -76.41) * mm, v(-86.06, -76.2) * mm, v(-85.86, -76.06) * mm, v(-85.65, -75.92) * mm, v(-85.35, -75.75) * mm, v(-84.8, -75.5) * mm, v(-84.17, -75.24) * mm, v(-83.48, -74.96) * mm, v(-83.03, -74.77) * mm, v(-82.67, -74.6) * mm, v(-82.3, -74.4) * mm, v(-81.86, -74.15) * mm, v(-81.36, -73.82) * mm, v(-80.74, -73.36) * mm, v(-80.02, -72.78) * mm, v(-79.2, -72.1) * mm, v(-78.56, -71.58) * mm, v(-78.05, -71.22) * mm, v(-77.67, -70.97) * mm, v(-77.28, -70.76) * mm, v(-76.87, -70.57) * mm, v(-76.42, -70.38) * mm, v(-75.8, -70.14) * mm, v(-74.95, -69.82) * mm, v(-73.88, -69.36) * mm, v(-72.8, -68.75) * mm, v(-72.12, -68.17) * mm, v(-71.8, -67.84) * mm]});
            skSolve(sketch);
        }
        {
            var Q0;
            Q0 = qSketchRegion(id + "F5", true);
            extrude(context, id + "F6", {"entities" : qUnion([Q0]), "operationType" : NewBodyOperationType.ADD, "depth" : 3 * mm, "offsetDistance" : 25 * mm});
        }
        {
            var Q0;
            Q0=makeQuery(id+"F3.imprint","IMPRINT",FACE,{"disambiguationData":[TD([[makeQuery(id+"F3.imprint","IMPRINT",EDGE,{"derivedFrom":sQuery(id+"F3.wireOp",EDGE,"E239")}),-1.0]])]});
            var sketch = newSketch(context, id + "F7", { "sketchPlane" : qUnion([Q0])});
            skLineSegment(sketch, "E270", {"start": v(-72.67, 67) * mm, "end": v(-64.94, 64.94) * mm});
            skLineSegment(sketch, "E271", {"start": v(-56.55, 62.7) * mm, "end": v(-54.74, 60.96) * mm});
            skLineSegment(sketch, "E272", {"start": v(-54.74, 60.96) * mm, "end": v(-63.24, 63.24) * mm});
            skLineSegment(sketch, "E273", {"start": v(-71.07, 65.34) * mm, "end": v(-72.67, 67) * mm});
            skLineSegment(sketch, "E274", {"start": v(-67, 72.67) * mm, "end": v(-64.94, 64.94) * mm});
            skLineSegment(sketch, "E275", {"start": v(-62.7, 56.55) * mm, "end": v(-60.96, 54.74) * mm});
            skLineSegment(sketch, "E276", {"start": v(-60.96, 54.74) * mm, "end": v(-63.24, 63.24) * mm});
            skLineSegment(sketch, "E277", {"start": v(-65.34, 71.07) * mm, "end": v(-67, 72.67) * mm});
            skLineSegment(sketch, "E278", {"start": v(-62.7, 56.55) * mm, "end": v(-56.55, 62.7) * mm, "construction": true});
            skLineSegment(sketch, "E279", {"start": v(-60.96, 54.74) * mm, "end": v(-54.74, 60.96) * mm, "construction": true});
            skPoint(sketch, "E280", {"position": v(-64.94, 64.94) * mm});
            skPoint(sketch, "E281", {"position": v(-63.24, 63.24) * mm});
            skPoint(sketch, "E282", {"position": v(-64.58, 63.6) * mm});
            skPoint(sketch, "E283", {"position": v(-63.6, 64.58) * mm});
            skLineSegment(sketch, "E284.trimOffspring", {"start": v(-64.58, 63.6) * mm, "end": v(-62.7, 56.55) * mm});
            skLineSegment(sketch, "E285.trimOffspring", {"start": v(-63.6, 64.58) * mm, "end": v(-56.55, 62.7) * mm});
            skLineSegment(sketch, "E286.trimOffspring", {"start": v(-64.58, 63.6) * mm, "end": v(-71.07, 65.34) * mm});
            skLineSegment(sketch, "E287.trimOffspring", {"start": v(-63.6, 64.58) * mm, "end": v(-65.34, 71.07) * mm});
            skLineSegment(sketch, "E288", {"start": v(-57.51, 51.12) * mm, "end": v(-55.92, 49.45) * mm});
            skLineSegment(sketch, "E289", {"start": v(-55.92, 49.45) * mm, "end": v(-48.42, 47.44) * mm});
            skLineSegment(sketch, "E290", {"start": v(-37.5, 44.52) * mm, "end": v(-39.3, 46.24) * mm});
            skLineSegment(sketch, "E291", {"start": v(-39.3, 46.24) * mm, "end": v(-47.44, 48.42) * mm});
            skLineSegment(sketch, "E292", {"start": v(-51.12, 57.51) * mm, "end": v(-49.45, 55.92) * mm});
            skLineSegment(sketch, "E293", {"start": v(-49.45, 55.92) * mm, "end": v(-47.44, 48.42) * mm});
            skLineSegment(sketch, "E294", {"start": v(-44.52, 37.5) * mm, "end": v(-46.24, 39.3) * mm});
            skLineSegment(sketch, "E295", {"start": v(-46.24, 39.3) * mm, "end": v(-48.42, 47.44) * mm});
            skLineSegment(sketch, "E296", {"start": v(-57.51, 51.12) * mm, "end": v(-51.12, 57.51) * mm, "construction": true});
            skLineSegment(sketch, "E297", {"start": v(-44.52, 37.5) * mm, "end": v(-37.5, 44.52) * mm, "construction": true});
            skLineSegment(sketch, "E298.trimOffspring", {"start": v(-48.78, 48.78) * mm, "end": v(-51.12, 57.51) * mm});
            skLineSegment(sketch, "E299.trimOffspring", {"start": v(-48.78, 48.78) * mm, "end": v(-57.51, 51.12) * mm});
            skLineSegment(sketch, "E300.trimOffspring", {"start": v(-47.08, 47.08) * mm, "end": v(-44.52, 37.5) * mm});
            skLineSegment(sketch, "E301.trimOffspring", {"start": v(-47.08, 47.08) * mm, "end": v(-37.5, 44.52) * mm});
            skLineSegment(sketch, "E302.MirrorCS", {"start": v(-37.5, -44.52) * mm, "end": v(-39.3, -46.24) * mm});
            skLineSegment(sketch, "E303.MirrorCS", {"start": v(-51.12, -57.51) * mm, "end": v(-49.45, -55.92) * mm});
            skLineSegment(sketch, "E304.MirrorCS", {"start": v(-57.51, -51.12) * mm, "end": v(-55.92, -49.45) * mm});
            skLineSegment(sketch, "E305.MirrorCS", {"start": v(-62.7, -56.55) * mm, "end": v(-60.96, -54.74) * mm});
            skLineSegment(sketch, "E306.MirrorCS", {"start": v(-44.52, -37.5) * mm, "end": v(-46.24, -39.3) * mm});
            skLineSegment(sketch, "E307.MirrorCS", {"start": v(-56.55, -62.7) * mm, "end": v(-54.74, -60.96) * mm});
            skLineSegment(sketch, "E308.MirrorCS", {"start": v(-72.67, -67) * mm, "end": v(-64.94, -64.94) * mm});
            skLineSegment(sketch, "E309.MirrorCS", {"start": v(-67, -72.67) * mm, "end": v(-64.94, -64.94) * mm});
            skLineSegment(sketch, "E310.MirrorCS", {"start": v(-71.07, -65.34) * mm, "end": v(-72.67, -67) * mm});
            skLineSegment(sketch, "E311.MirrorCS", {"start": v(-65.34, -71.07) * mm, "end": v(-67, -72.67) * mm});
            skLineSegment(sketch, "E312.MirrorCS", {"start": v(-57.51, -51.12) * mm, "end": v(-51.12, -57.51) * mm, "construction": true});
            skLineSegment(sketch, "E313.MirrorCS", {"start": v(-48.78, -48.78) * mm, "end": v(-51.12, -57.51) * mm});
            skLineSegment(sketch, "E314.MirrorCS", {"start": v(-47.08, -47.08) * mm, "end": v(-37.5, -44.52) * mm});
            skLineSegment(sketch, "E315.MirrorCS", {"start": v(-63.6, -64.58) * mm, "end": v(-65.34, -71.07) * mm});
            skLineSegment(sketch, "E316.MirrorCS", {"start": v(-44.52, -37.5) * mm, "end": v(-37.5, -44.52) * mm, "construction": true});
            skPoint(sketch, "E317.MirrorP", {"position": v(-64.94, -64.94) * mm});
            skLineSegment(sketch, "E318.MirrorCS", {"start": v(-60.96, -54.74) * mm, "end": v(-54.74, -60.96) * mm, "construction": true});
            skLineSegment(sketch, "E319.MirrorCS", {"start": v(-62.7, -56.55) * mm, "end": v(-56.55, -62.7) * mm, "construction": true});
            skLineSegment(sketch, "E320.MirrorCS", {"start": v(-54.74, -60.96) * mm, "end": v(-63.24, -63.24) * mm});
            skLineSegment(sketch, "E321.MirrorCS", {"start": v(-63.6, -64.58) * mm, "end": v(-56.55, -62.7) * mm});
            skPoint(sketch, "E322.MirrorP", {"position": v(-63.24, -63.24) * mm});
            skLineSegment(sketch, "E323.MirrorCS", {"start": v(-39.3, -46.24) * mm, "end": v(-47.44, -48.42) * mm});
            skLineSegment(sketch, "E324.MirrorCS", {"start": v(-60.96, -54.74) * mm, "end": v(-63.24, -63.24) * mm});
            skLineSegment(sketch, "E325.MirrorCS", {"start": v(-46.24, -39.3) * mm, "end": v(-48.42, -47.44) * mm});
            skPoint(sketch, "E326.MirrorP", {"position": v(-64.58, -63.6) * mm});
            skPoint(sketch, "E327.MirrorP", {"position": v(-63.6, -64.58) * mm});
            skLineSegment(sketch, "E328.MirrorCS", {"start": v(-49.45, -55.92) * mm, "end": v(-47.44, -48.42) * mm});
            skLineSegment(sketch, "E329.MirrorCS", {"start": v(-64.58, -63.6) * mm, "end": v(-71.07, -65.34) * mm});
            skLineSegment(sketch, "E330.MirrorCS", {"start": v(-55.92, -49.45) * mm, "end": v(-48.42, -47.44) * mm});
            skLineSegment(sketch, "E331.MirrorCS", {"start": v(-64.58, -63.6) * mm, "end": v(-62.7, -56.55) * mm});
            skLineSegment(sketch, "E332.MirrorCS", {"start": v(-47.08, -47.08) * mm, "end": v(-44.52, -37.5) * mm});
            skLineSegment(sketch, "E333.MirrorCS", {"start": v(-48.78, -48.78) * mm, "end": v(-57.51, -51.12) * mm});
            skLineSegment(sketch, "E334.MirrorCS", {"start": v(56.55, 62.7) * mm, "end": v(54.74, 60.96) * mm});
            skLineSegment(sketch, "E335.MirrorCS", {"start": v(54.74, 60.96) * mm, "end": v(63.24, 63.24) * mm});
            skLineSegment(sketch, "E336.MirrorCS", {"start": v(60.96, 54.74) * mm, "end": v(63.24, 63.24) * mm});
            skLineSegment(sketch, "E337.MirrorCS", {"start": v(62.7, 56.55) * mm, "end": v(56.55, 62.7) * mm, "construction": true});
            skLineSegment(sketch, "E338.MirrorCS", {"start": v(63.6, 64.58) * mm, "end": v(56.55, 62.7) * mm});
            skLineSegment(sketch, "E339.MirrorCS", {"start": v(62.7, 56.55) * mm, "end": v(60.96, 54.74) * mm});
            skLineSegment(sketch, "E340.MirrorCS", {"start": v(54.74, -60.96) * mm, "end": v(63.24, -63.24) * mm});
            skLineSegment(sketch, "E341.MirrorCS", {"start": v(51.12, 57.51) * mm, "end": v(49.45, 55.92) * mm});
            skLineSegment(sketch, "E342.MirrorCS", {"start": v(60.96, -54.74) * mm, "end": v(63.24, -63.24) * mm});
            skLineSegment(sketch, "E343.MirrorCS", {"start": v(37.5, 44.52) * mm, "end": v(39.3, 46.24) * mm});
            skLineSegment(sketch, "E344.MirrorCS", {"start": v(63.6, 64.58) * mm, "end": v(65.34, 71.07) * mm});
            skLineSegment(sketch, "E345.MirrorCS", {"start": v(64.58, 63.6) * mm, "end": v(62.7, 56.55) * mm});
            skLineSegment(sketch, "E346.MirrorCS", {"start": v(57.51, 51.12) * mm, "end": v(51.12, 57.51) * mm, "construction": true});
            skLineSegment(sketch, "E347.MirrorCS", {"start": v(57.51, 51.12) * mm, "end": v(55.92, 49.45) * mm});
            skLineSegment(sketch, "E348.MirrorCS", {"start": v(56.55, -62.7) * mm, "end": v(54.74, -60.96) * mm});
            skLineSegment(sketch, "E349.MirrorCS", {"start": v(60.96, 54.74) * mm, "end": v(54.74, 60.96) * mm, "construction": true});
            skLineSegment(sketch, "E350.MirrorCS", {"start": v(44.52, -37.5) * mm, "end": v(46.24, -39.3) * mm});
            skLineSegment(sketch, "E351.MirrorCS", {"start": v(64.58, -63.6) * mm, "end": v(71.07, -65.34) * mm});
            skLineSegment(sketch, "E352.MirrorCS", {"start": v(46.24, -39.3) * mm, "end": v(48.42, -47.44) * mm});
            skLineSegment(sketch, "E353.MirrorCS", {"start": v(44.52, 37.5) * mm, "end": v(46.24, 39.3) * mm});
            skLineSegment(sketch, "E354.MirrorCS", {"start": v(39.3, -46.24) * mm, "end": v(47.44, -48.42) * mm});
            skLineSegment(sketch, "E355.MirrorCS", {"start": v(62.7, -56.55) * mm, "end": v(60.96, -54.74) * mm});
            skLineSegment(sketch, "E356.MirrorCS", {"start": v(57.51, -51.12) * mm, "end": v(51.12, -57.51) * mm, "construction": true});
            skLineSegment(sketch, "E357.MirrorCS", {"start": v(63.6, -64.58) * mm, "end": v(56.55, -62.7) * mm});
            skLineSegment(sketch, "E358.MirrorCS", {"start": v(60.96, -54.74) * mm, "end": v(54.74, -60.96) * mm, "construction": true});
            skLineSegment(sketch, "E359.MirrorCS", {"start": v(57.51, -51.12) * mm, "end": v(55.92, -49.45) * mm});
            skLineSegment(sketch, "E360.MirrorCS", {"start": v(47.08, -47.08) * mm, "end": v(37.5, -44.52) * mm});
            skLineSegment(sketch, "E361.MirrorCS", {"start": v(62.7, -56.55) * mm, "end": v(56.55, -62.7) * mm, "construction": true});
            skLineSegment(sketch, "E362.MirrorCS", {"start": v(71.07, 65.34) * mm, "end": v(72.67, 67) * mm});
            skLineSegment(sketch, "E363.MirrorCS", {"start": v(64.58, 63.6) * mm, "end": v(71.07, 65.34) * mm});
            skLineSegment(sketch, "E364.MirrorCS", {"start": v(47.08, -47.08) * mm, "end": v(44.52, -37.5) * mm});
            skLineSegment(sketch, "E365.MirrorCS", {"start": v(64.58, -63.6) * mm, "end": v(62.7, -56.55) * mm});
            skLineSegment(sketch, "E366.MirrorCS", {"start": v(44.52, 37.5) * mm, "end": v(37.5, 44.52) * mm, "construction": true});
            skLineSegment(sketch, "E367.MirrorCS", {"start": v(37.5, -44.52) * mm, "end": v(39.3, -46.24) * mm});
            skLineSegment(sketch, "E368.MirrorCS", {"start": v(44.52, -37.5) * mm, "end": v(37.5, -44.52) * mm, "construction": true});
            skLineSegment(sketch, "E369.MirrorCS", {"start": v(51.12, -57.51) * mm, "end": v(49.45, -55.92) * mm});
            skLineSegment(sketch, "E370.MirrorCS", {"start": v(63.6, -64.58) * mm, "end": v(65.34, -71.07) * mm});
            skLineSegment(sketch, "E371.MirrorCS", {"start": v(39.3, 46.24) * mm, "end": v(47.44, 48.42) * mm});
            skLineSegment(sketch, "E372.MirrorCS", {"start": v(48.78, 48.78) * mm, "end": v(51.12, 57.51) * mm});
            skLineSegment(sketch, "E373.MirrorCS", {"start": v(71.07, -65.34) * mm, "end": v(72.67, -67) * mm});
            skLineSegment(sketch, "E374.MirrorCS", {"start": v(67, 72.67) * mm, "end": v(64.94, 64.94) * mm});
            skLineSegment(sketch, "E375.MirrorCS", {"start": v(72.67, 67) * mm, "end": v(64.94, 64.94) * mm});
            skLineSegment(sketch, "E376.MirrorCS", {"start": v(46.24, 39.3) * mm, "end": v(48.42, 47.44) * mm});
            skLineSegment(sketch, "E377.MirrorCS", {"start": v(47.08, 47.08) * mm, "end": v(44.52, 37.5) * mm});
            skLineSegment(sketch, "E378.MirrorCS", {"start": v(72.67, -67) * mm, "end": v(64.94, -64.94) * mm});
            skLineSegment(sketch, "E379.MirrorCS", {"start": v(47.08, 47.08) * mm, "end": v(37.5, 44.52) * mm});
            skLineSegment(sketch, "E380.MirrorCS", {"start": v(49.45, 55.92) * mm, "end": v(47.44, 48.42) * mm});
            skLineSegment(sketch, "E381.MirrorCS", {"start": v(65.34, 71.07) * mm, "end": v(67, 72.67) * mm});
            skLineSegment(sketch, "E382.MirrorCS", {"start": v(48.78, -48.78) * mm, "end": v(51.12, -57.51) * mm});
            skLineSegment(sketch, "E383.MirrorCS", {"start": v(48.78, -48.78) * mm, "end": v(57.51, -51.12) * mm});
            skLineSegment(sketch, "E384.MirrorCS", {"start": v(55.92, -49.45) * mm, "end": v(48.42, -47.44) * mm});
            skLineSegment(sketch, "E385.MirrorCS", {"start": v(67, -72.67) * mm, "end": v(64.94, -64.94) * mm});
            skLineSegment(sketch, "E386.MirrorCS", {"start": v(48.78, 48.78) * mm, "end": v(57.51, 51.12) * mm});
            skLineSegment(sketch, "E387.MirrorCS", {"start": v(55.92, 49.45) * mm, "end": v(48.42, 47.44) * mm});
            skLineSegment(sketch, "E388.MirrorCS", {"start": v(49.45, -55.92) * mm, "end": v(47.44, -48.42) * mm});
            skLineSegment(sketch, "E389.MirrorCS", {"start": v(65.34, -71.07) * mm, "end": v(67, -72.67) * mm});
            skPoint(sketch, "E390.MirrorP", {"position": v(64.94, 64.94) * mm});
            skPoint(sketch, "E391.MirrorP", {"position": v(63.6, -64.58) * mm});
            skPoint(sketch, "E392.MirrorP", {"position": v(63.6, 64.58) * mm});
            skPoint(sketch, "E393.MirrorP", {"position": v(64.94, -64.94) * mm});
            skPoint(sketch, "E394.MirrorP", {"position": v(64.58, 63.6) * mm});
            skPoint(sketch, "E395.MirrorP", {"position": v(63.24, -63.24) * mm});
            skPoint(sketch, "E396.MirrorP", {"position": v(64.58, -63.6) * mm});
            skPoint(sketch, "E397.MirrorP", {"position": v(63.24, 63.24) * mm});
            skSolve(sketch);
        }
        {
            var Q0;
            Q0 = qSketchRegion(id + "F7", true);
            extrude(context, id + "F8", {"entities" : qUnion([Q0]), "operationType" : NewBodyOperationType.ADD, "depth" : 2 * mm, "offsetDistance" : 25 * mm});
        }
    });
